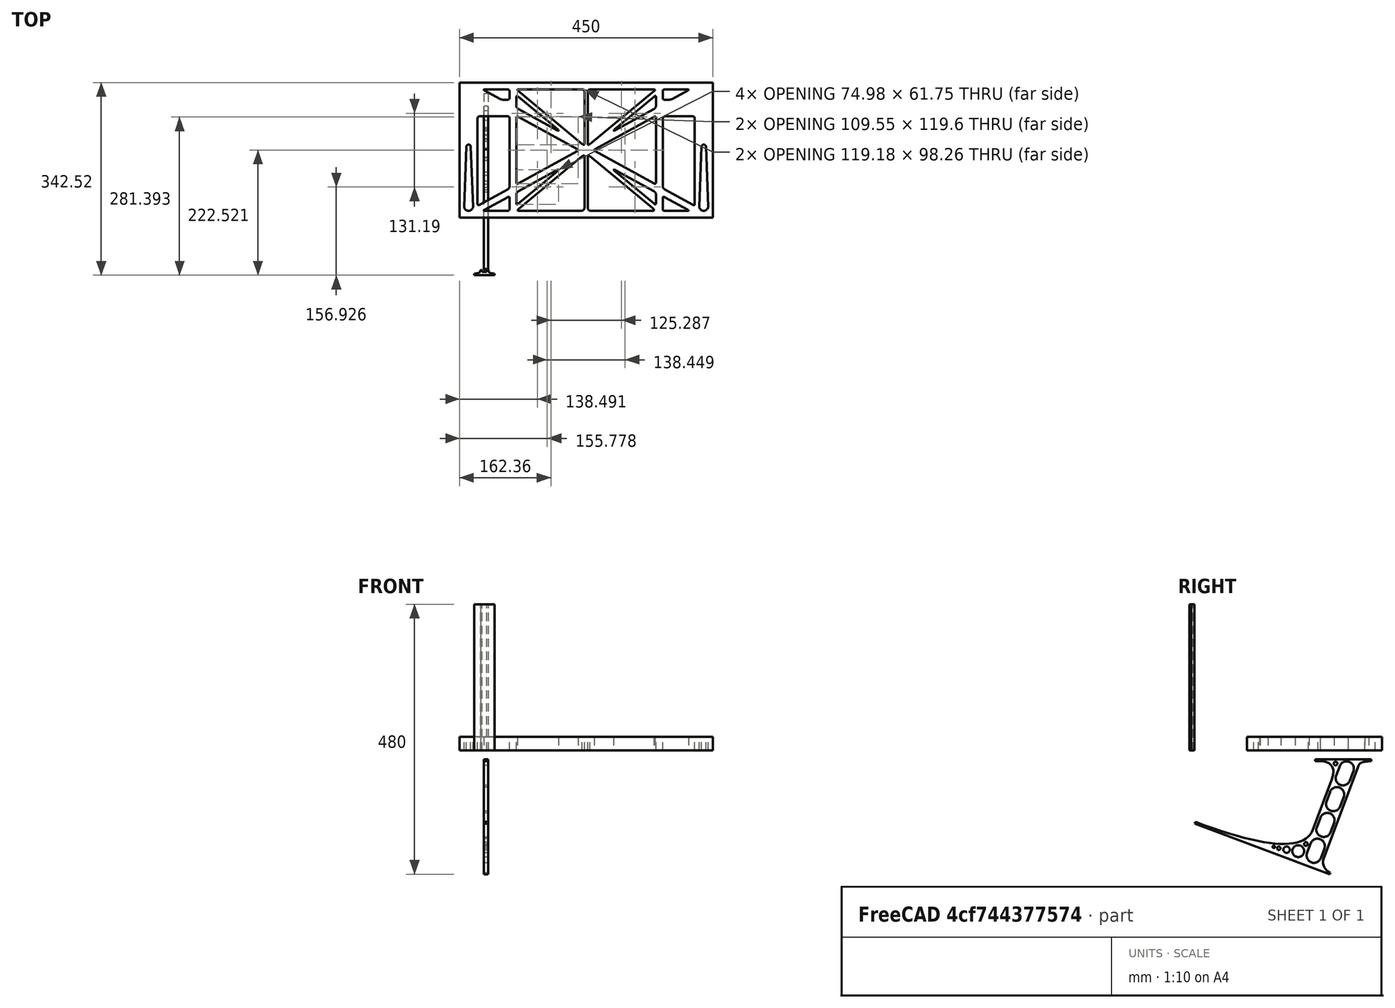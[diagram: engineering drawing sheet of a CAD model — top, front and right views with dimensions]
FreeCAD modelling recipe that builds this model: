
FCSTD DOCUMENT  (FreeCAD 0.19R0.19.2)
Label: laptopStand164FCStd
License: All rights reserved
LicenseURL: http://en.wikipedia.org/wiki/All_rights_reserved
objects: Sketcher::SketchObject×4, Part::Extrusion×3
note: 7 computed .brp shape members not serialized (recipe doc carries the construction recipe); baked Part::Feature solids carry a one-line shape summary decoded from their .brp

FEATURE [Sketcher::SketchObject] Sketch
  FullyConstrained = false
  sketch-geometry (349):
    g0: LineSegment StartX=-10.9272 StartY=-82.7794 StartZ=0 EndX=46.0728 EndY=-51.4823 EndZ=0
    g1: LineSegment StartX=-10.9272 StartY=76.4095 StartZ=0 EndX=-10.9272 EndY=-82.7794 EndZ=0
    g2: LineSegment StartX=46.0728 StartY=76.4095 StartZ=0 EndX=46.0728 EndY=-51.4823 EndZ=0
    g3: LineSegment StartX=-42.9272 StartY=136.221 StartZ=0 EndX=-42.9272 EndY=-103.779 EndZ=0
    g4: LineSegment StartX=407.073 StartY=136.221 StartZ=0 EndX=407.073 EndY=-103.779 EndZ=0
    g5: ArcOfCircle CenterX=-26.9272 CenterY=-83.7794 CenterZ=0 NormalX=0 NormalY=0 NormalZ=1 AngleXU=0 Radius=8 StartAngle=3.14159 EndAngle=6.28319
    g6: ArcOfCircle CenterX=391.073 CenterY=22.1087 CenterZ=0 NormalX=0 NormalY=0 NormalZ=1 AngleXU=0 Radius=8 StartAngle=-4.4e-15 EndAngle=3.14159
    g7: LineSegment StartX=399.073 StartY=22.1087 StartZ=0 EndX=399.073 EndY=-83.7794 EndZ=0
    g8: LineSegment StartX=383.073 StartY=22.1087 StartZ=0 EndX=383.073 EndY=-83.7794 EndZ=0
    g9: ArcOfCircle CenterX=391.073 CenterY=-83.7794 CenterZ=0 NormalX=0 NormalY=0 NormalZ=1 AngleXU=0 Radius=8 StartAngle=3.14159 EndAngle=6.28319
    g10: Circle CenterX=175.022 CenterY=27.0628 CenterZ=0 NormalX=0 NormalY=0 NormalZ=1 AngleXU=0 Radius=1
    g11: Circle CenterX=179.022 CenterY=24.8665 CenterZ=0 NormalX=0 NormalY=0 NormalZ=1 AngleXU=0 Radius=1
    g12: Circle CenterX=179.022 CenterY=27.0628 CenterZ=0 NormalX=0 NormalY=0 NormalZ=1 AngleXU=0 Radius=1
    g13: BSplineCurve PolesCount=3 KnotsCount=2 Degree=2 IsPeriodic=0
    g14: GeomPoint X=175.022 Y=27.0628 Z=0
    g15: GeomPoint X=179.022 Y=27.0628 Z=0
    g16: Circle CenterX=189.124 CenterY=27.0628 CenterZ=0 NormalX=0 NormalY=0 NormalZ=1 AngleXU=0 Radius=1
    g17: Circle CenterX=185.124 CenterY=24.8665 CenterZ=0 NormalX=0 NormalY=0 NormalZ=1 AngleXU=0 Radius=1
    g18: Circle CenterX=185.124 CenterY=27.0628 CenterZ=0 NormalX=0 NormalY=0 NormalZ=1 AngleXU=0 Radius=1
    g19: BSplineCurve PolesCount=3 KnotsCount=2 Degree=2 IsPeriodic=0
    g20: GeomPoint X=189.124 Y=27.0628 Z=0
    g21: GeomPoint X=185.124 Y=27.0628 Z=0
    g22: Circle CenterX=175.022 CenterY=5.37834 CenterZ=0 NormalX=0 NormalY=0 NormalZ=1 AngleXU=0 Radius=1
    g23: Circle CenterX=179.022 CenterY=7.57463 CenterZ=0 NormalX=0 NormalY=0 NormalZ=1 AngleXU=0 Radius=1
    g24: Circle CenterX=179.022 CenterY=5.34704 CenterZ=0 NormalX=0 NormalY=0 NormalZ=1 AngleXU=0 Radius=1
    g25: BSplineCurve PolesCount=3 KnotsCount=2 Degree=2 IsPeriodic=0
    g26: GeomPoint X=175.022 Y=5.37834 Z=0
    g27: GeomPoint X=179.022 Y=5.34704 Z=0
    g28: Circle CenterX=189.124 CenterY=5.37834 CenterZ=0 NormalX=0 NormalY=0 NormalZ=1 AngleXU=0 Radius=1
    g29: Circle CenterX=185.124 CenterY=7.57463 CenterZ=0 NormalX=0 NormalY=0 NormalZ=1 AngleXU=0 Radius=1
    g30: Circle CenterX=185.124 CenterY=5.34704 CenterZ=0 NormalX=0 NormalY=0 NormalZ=1 AngleXU=0 Radius=1
    g31: BSplineCurve PolesCount=3 KnotsCount=2 Degree=2 IsPeriodic=0
    g32: GeomPoint X=189.124 Y=5.37834 Z=0
    g33: GeomPoint X=185.124 Y=5.34704 Z=0
    g34: Circle CenterX=165.871 CenterY=18.1458 CenterZ=0 NormalX=0 NormalY=0 NormalZ=1 AngleXU=0 Radius=1
    g35: Circle CenterX=169.377 CenterY=16.2206 CenterZ=0 NormalX=0 NormalY=0 NormalZ=1 AngleXU=0 Radius=1
    g36: Circle CenterX=165.871 CenterY=14.2954 CenterZ=0 NormalX=0 NormalY=0 NormalZ=1 AngleXU=0 Radius=1
    g37: BSplineCurve PolesCount=3 KnotsCount=2 Degree=2 IsPeriodic=0
    g38: GeomPoint X=165.871 Y=18.1458 Z=0
    g39: GeomPoint X=165.871 Y=14.2954 Z=0
    g40: Circle CenterX=198.275 CenterY=18.1458 CenterZ=0 NormalX=0 NormalY=0 NormalZ=1 AngleXU=0 Radius=1
    g41: Circle CenterX=194.768 CenterY=16.2206 CenterZ=0 NormalX=0 NormalY=0 NormalZ=1 AngleXU=0 Radius=1
    g42: Circle CenterX=198.275 CenterY=14.2954 CenterZ=0 NormalX=0 NormalY=0 NormalZ=1 AngleXU=0 Radius=1
    g43: BSplineCurve PolesCount=3 KnotsCount=2 Degree=2 IsPeriodic=0
    g44: GeomPoint X=198.275 Y=18.1458 Z=0
    g45: GeomPoint X=198.275 Y=14.2954 Z=0
    g46: LineSegment StartX=407.073 StartY=-103.779 StartZ=0 EndX=-42.9272 EndY=-103.779 EndZ=0
    g47: LineSegment StartX=407.073 StartY=136.221 StartZ=0 EndX=-42.9272 EndY=136.221 EndZ=0
    g48: LineSegment StartX=46.0728 StartY=76.4095 StartZ=0 EndX=-10.9272 EndY=76.4095 EndZ=0
    g49: Circle CenterX=125.607 CenterY=54.1951 CenterZ=0 NormalX=0 NormalY=0 NormalZ=1 AngleXU=0 Radius=1
    g50: Circle CenterX=139.632 CenterY=46.4944 CenterZ=0 NormalX=0 NormalY=0 NormalZ=1 AngleXU=0 Radius=1
    g51: Circle CenterX=127.326 CenterY=56.7187 CenterZ=0 NormalX=0 NormalY=0 NormalZ=1 AngleXU=0 Radius=1
    g52: BSplineCurve PolesCount=3 KnotsCount=2 Degree=2 IsPeriodic=0
    g53: GeomPoint X=125.607 Y=54.1951 Z=0
    g54: GeomPoint X=127.326 Y=56.7187 Z=0
    g55: Circle CenterX=236.821 CenterY=56.7187 CenterZ=0 NormalX=0 NormalY=0 NormalZ=1 AngleXU=0 Radius=1
    g56: Circle CenterX=224.513 CenterY=46.4944 CenterZ=0 NormalX=0 NormalY=0 NormalZ=1 AngleXU=0 Radius=1
    g57: Circle CenterX=238.538 CenterY=54.1951 CenterZ=0 NormalX=0 NormalY=0 NormalZ=1 AngleXU=0 Radius=1
    g58: BSplineCurve PolesCount=3 KnotsCount=2 Degree=2 IsPeriodic=0
    g59: GeomPoint X=236.821 Y=56.7187 Z=0
    g60: GeomPoint X=238.538 Y=54.1951 Z=0
    g61: Circle CenterX=238.538 CenterY=-21.7539 CenterZ=0 NormalX=0 NormalY=0 NormalZ=1 AngleXU=0 Radius=1
    g62: Circle CenterX=224.513 CenterY=-14.0532 CenterZ=0 NormalX=0 NormalY=0 NormalZ=1 AngleXU=0 Radius=1
    g63: Circle CenterX=236.821 CenterY=-24.2775 CenterZ=0 NormalX=0 NormalY=0 NormalZ=1 AngleXU=0 Radius=1
    g64: BSplineCurve PolesCount=3 KnotsCount=2 Degree=2 IsPeriodic=0
    g65: GeomPoint X=238.538 Y=-21.7539 Z=0
    g66: GeomPoint X=236.821 Y=-24.2775 Z=0
    g67: Circle CenterX=125.607 CenterY=-21.7539 CenterZ=0 NormalX=0 NormalY=0 NormalZ=1 AngleXU=0 Radius=1
    g68: Circle CenterX=139.632 CenterY=-14.0532 CenterZ=0 NormalX=0 NormalY=0 NormalZ=1 AngleXU=0 Radius=1
    g69: Circle CenterX=127.325 CenterY=-24.2775 CenterZ=0 NormalX=0 NormalY=0 NormalZ=1 AngleXU=0 Radius=1
    g70: BSplineCurve PolesCount=3 KnotsCount=2 Degree=2 IsPeriodic=0
    g71: GeomPoint X=125.607 Y=-21.7539 Z=0
    g72: GeomPoint X=127.325 Y=-24.2775 Z=0
    g73: Circle CenterX=302.996 CenterY=111.695 CenterZ=0 NormalX=0 NormalY=0 NormalZ=1 AngleXU=0 Radius=1
    g74: Circle CenterX=306.073 CenterY=114.251 CenterZ=0 NormalX=0 NormalY=0 NormalZ=1 AngleXU=0 Radius=1
    g75: Circle CenterX=306.073 CenterY=110.251 CenterZ=0 NormalX=0 NormalY=0 NormalZ=1 AngleXU=0 Radius=1
    g76: BSplineCurve PolesCount=3 KnotsCount=2 Degree=2 IsPeriodic=0
    g77: GeomPoint X=302.996 Y=111.695 Z=0
    g78: GeomPoint X=306.073 Y=110.251 Z=0
    g79: Circle CenterX=306.073 CenterY=95.2763 CenterZ=0 NormalX=0 NormalY=0 NormalZ=1 AngleXU=0 Radius=1
    g80: Circle CenterX=306.073 CenterY=91.2763 CenterZ=0 NormalX=0 NormalY=0 NormalZ=1 AngleXU=0 Radius=1
    g81: Circle CenterX=302.567 CenterY=89.3511 CenterZ=0 NormalX=0 NormalY=0 NormalZ=1 AngleXU=0 Radius=1
    g82: BSplineCurve PolesCount=3 KnotsCount=2 Degree=2 IsPeriodic=0
    g83: GeomPoint X=306.073 Y=95.2763 Z=0
    g84: GeomPoint X=302.567 Y=89.3511 Z=0
    g85: LineSegment StartX=306.073 StartY=110.251 StartZ=0 EndX=306.073 EndY=95.2763 EndZ=0
    g86: LineSegment StartX=302.996 StartY=111.695 StartZ=0 EndX=236.821 EndY=56.7187 EndZ=0
    g87: LineSegment StartX=238.538 StartY=54.1951 StartZ=0 EndX=302.567 EndY=89.3511 EndZ=0
    g88: Circle CenterX=61.1496 CenterY=111.695 CenterZ=0 NormalX=0 NormalY=0 NormalZ=1 AngleXU=0 Radius=1
    g89: Circle CenterX=58.0728 CenterY=114.251 CenterZ=0 NormalX=0 NormalY=0 NormalZ=1 AngleXU=0 Radius=1
    g90: Circle CenterX=58.0728 CenterY=110.251 CenterZ=0 NormalX=0 NormalY=0 NormalZ=1 AngleXU=0 Radius=1
    g91: BSplineCurve PolesCount=3 KnotsCount=2 Degree=2 IsPeriodic=0
    g92: GeomPoint X=61.1496 Y=111.695 Z=0
    g93: GeomPoint X=58.0728 Y=110.251 Z=0
    g94: Circle CenterX=61.5791 CenterY=89.3511 CenterZ=0 NormalX=0 NormalY=0 NormalZ=1 AngleXU=0 Radius=1
    g95: Circle CenterX=58.0728 CenterY=91.2763 CenterZ=0 NormalX=0 NormalY=0 NormalZ=1 AngleXU=0 Radius=1
    g96: Circle CenterX=58.0728 CenterY=95.2763 CenterZ=0 NormalX=0 NormalY=0 NormalZ=1 AngleXU=0 Radius=1
    g97: BSplineCurve PolesCount=3 KnotsCount=2 Degree=2 IsPeriodic=0
    g98: GeomPoint X=61.5791 Y=89.3511 Z=0
    g99: GeomPoint X=58.0728 Y=95.2763 Z=0
    g100: LineSegment StartX=58.0728 StartY=110.251 StartZ=0 EndX=58.0728 EndY=95.2763 EndZ=0
    g101: LineSegment StartX=61.1496 StartY=111.695 StartZ=0 EndX=127.326 EndY=56.7187 EndZ=0
    g102: LineSegment StartX=125.607 StartY=54.1951 StartZ=0 EndX=61.5791 EndY=89.3511 EndZ=0
    g103: Circle CenterX=61.5791 CenterY=-56.9099 CenterZ=0 NormalX=0 NormalY=0 NormalZ=1 AngleXU=0 Radius=1
    g104: Circle CenterX=58.0728 CenterY=-58.8351 CenterZ=0 NormalX=0 NormalY=0 NormalZ=1 AngleXU=0 Radius=1
    g105: Circle CenterX=58.0728 CenterY=-62.8351 CenterZ=0 NormalX=0 NormalY=0 NormalZ=1 AngleXU=0 Radius=1
    g106: BSplineCurve PolesCount=3 KnotsCount=2 Degree=2 IsPeriodic=0
    g107: GeomPoint X=61.5791 Y=-56.9099 Z=0
    g108: GeomPoint X=58.0728 Y=-62.8351 Z=0
    g109: Circle CenterX=58.0728 CenterY=-77.8102 CenterZ=0 NormalX=0 NormalY=0 NormalZ=1 AngleXU=0 Radius=1
    g110: Circle CenterX=58.0728 CenterY=-81.8102 CenterZ=0 NormalX=0 NormalY=0 NormalZ=1 AngleXU=0 Radius=1
    g111: Circle CenterX=61.1496 CenterY=-79.2541 CenterZ=0 NormalX=0 NormalY=0 NormalZ=1 AngleXU=0 Radius=1
    g112: BSplineCurve PolesCount=3 KnotsCount=2 Degree=2 IsPeriodic=0
    g113: GeomPoint X=58.0728 Y=-77.8102 Z=0
    g114: GeomPoint X=61.1496 Y=-79.2541 Z=0
    g115: LineSegment StartX=58.0728 StartY=-62.8351 StartZ=0 EndX=58.0728 EndY=-77.8102 EndZ=0
    g116: LineSegment StartX=61.1496 StartY=-79.2541 StartZ=0 EndX=127.325 EndY=-24.2775 EndZ=0
    g117: LineSegment StartX=125.607 StartY=-21.7539 StartZ=0 EndX=61.5791 EndY=-56.9099 EndZ=0
    g118: Circle CenterX=302.567 CenterY=-56.9099 CenterZ=0 NormalX=0 NormalY=0 NormalZ=1 AngleXU=0 Radius=1
    g119: Circle CenterX=306.073 CenterY=-58.8351 CenterZ=0 NormalX=0 NormalY=0 NormalZ=1 AngleXU=0 Radius=1
    g120: Circle CenterX=306.073 CenterY=-62.8351 CenterZ=0 NormalX=0 NormalY=0 NormalZ=1 AngleXU=0 Radius=1
    g121: BSplineCurve PolesCount=3 KnotsCount=2 Degree=2 IsPeriodic=0
    g122: GeomPoint X=302.567 Y=-56.9099 Z=0
    g123: GeomPoint X=306.073 Y=-62.8351 Z=0
    g124: Circle CenterX=302.996 CenterY=-79.2541 CenterZ=0 NormalX=0 NormalY=0 NormalZ=1 AngleXU=0 Radius=1
    g125: Circle CenterX=306.073 CenterY=-81.8102 CenterZ=0 NormalX=0 NormalY=0 NormalZ=1 AngleXU=0 Radius=1
    g126: Circle CenterX=306.073 CenterY=-77.8102 CenterZ=0 NormalX=0 NormalY=0 NormalZ=1 AngleXU=0 Radius=1
    g127: BSplineCurve PolesCount=3 KnotsCount=2 Degree=2 IsPeriodic=0
    g128: GeomPoint X=302.996 Y=-79.2541 Z=0
    g129: GeomPoint X=306.073 Y=-77.8102 Z=0
    g130: LineSegment StartX=306.073 StartY=-62.8351 StartZ=0 EndX=306.073 EndY=-77.8102 EndZ=0
    g131: LineSegment StartX=302.996 StartY=-79.2541 StartZ=0 EndX=236.821 EndY=-24.2775 EndZ=0
    g132: LineSegment StartX=238.538 StartY=-21.7539 StartZ=0 EndX=302.567 EndY=-56.9099 EndZ=0
    g133: Circle CenterX=61.6457 CenterY=-88.8112 CenterZ=0 NormalX=0 NormalY=0 NormalZ=1 AngleXU=0 Radius=1
    g134: Circle CenterX=58.0728 CenterY=-91.7794 CenterZ=0 NormalX=0 NormalY=0 NormalZ=1 AngleXU=0 Radius=1
    g135: Circle CenterX=63.9135 CenterY=-91.7794 CenterZ=0 NormalX=0 NormalY=0 NormalZ=1 AngleXU=0 Radius=1
    g136: BSplineCurve PolesCount=3 KnotsCount=2 Degree=2 IsPeriodic=0
    g137: GeomPoint X=61.6457 Y=-88.8112 Z=0
    g138: GeomPoint X=63.9135 Y=-91.7794 Z=0
    g139: Circle CenterX=179.022 CenterY=-85.8163 CenterZ=0 NormalX=0 NormalY=0 NormalZ=1 AngleXU=0 Radius=1
    g140: Circle CenterX=179.022 CenterY=-91.7794 CenterZ=0 NormalX=0 NormalY=0 NormalZ=1 AngleXU=0 Radius=1
    g141: Circle CenterX=171.895 CenterY=-91.7794 CenterZ=0 NormalX=0 NormalY=0 NormalZ=1 AngleXU=0 Radius=1
    g142: BSplineCurve PolesCount=3 KnotsCount=2 Degree=2 IsPeriodic=0
    g143: GeomPoint X=179.022 Y=-85.8163 Z=0
    g144: GeomPoint X=171.895 Y=-91.7794 Z=0
    g145: Circle CenterX=185.124 CenterY=-86.2028 CenterZ=0 NormalX=0 NormalY=0 NormalZ=1 AngleXU=0 Radius=1
    g146: Circle CenterX=185.124 CenterY=-91.7794 CenterZ=0 NormalX=0 NormalY=0 NormalZ=1 AngleXU=0 Radius=1
    g147: Circle CenterX=191.747 CenterY=-91.7794 CenterZ=0 NormalX=0 NormalY=0 NormalZ=1 AngleXU=0 Radius=1
    g148: BSplineCurve PolesCount=3 KnotsCount=2 Degree=2 IsPeriodic=0
    g149: GeomPoint X=185.124 Y=-86.2028 Z=0
    g150: GeomPoint X=191.747 Y=-91.7794 Z=0
    g151: Circle CenterX=299.888 CenterY=-86.6413 CenterZ=0 NormalX=0 NormalY=0 NormalZ=1 AngleXU=0 Radius=1
    g152: Circle CenterX=306.073 CenterY=-91.7794 CenterZ=0 NormalX=0 NormalY=0 NormalZ=1 AngleXU=0 Radius=1
    g153: Circle CenterX=298.776 CenterY=-91.7794 CenterZ=0 NormalX=0 NormalY=0 NormalZ=1 AngleXU=0 Radius=1
    g154: BSplineCurve PolesCount=3 KnotsCount=2 Degree=2 IsPeriodic=0
    g155: GeomPoint X=299.888 Y=-86.6413 Z=0
    g156: GeomPoint X=298.776 Y=-91.7794 Z=0
    g157: LineSegment StartX=189.124 StartY=5.37834 StartZ=0 EndX=299.888 EndY=-86.6413 EndZ=0
    g158: LineSegment StartX=298.776 StartY=-91.7794 StartZ=0 EndX=191.747 EndY=-91.7794 EndZ=0
    g159: LineSegment StartX=185.124 StartY=-86.2028 StartZ=0 EndX=185.124 EndY=5.34704 EndZ=0
    g160: LineSegment StartX=179.022 StartY=5.34704 StartZ=0 EndX=179.022 EndY=-85.8163 EndZ=0
    g161: LineSegment StartX=171.895 StartY=-91.7794 StartZ=0 EndX=63.9135 EndY=-91.7794 EndZ=0
    g162: LineSegment StartX=61.6457 StartY=-88.8112 StartZ=0 EndX=175.022 EndY=5.37834 EndZ=0
    g163: Circle CenterX=302.073 CenterY=124.221 CenterZ=0 NormalX=0 NormalY=0 NormalZ=1 AngleXU=0 Radius=1
    g164: Circle CenterX=306.073 CenterY=124.221 CenterZ=0 NormalX=0 NormalY=0 NormalZ=1 AngleXU=0 Radius=1
    g165: Circle CenterX=302.996 CenterY=121.665 CenterZ=0 NormalX=0 NormalY=0 NormalZ=1 AngleXU=0 Radius=1
    g166: BSplineCurve PolesCount=3 KnotsCount=2 Degree=2 IsPeriodic=0
    g167: GeomPoint X=302.073 Y=124.221 Z=0
    g168: GeomPoint X=302.996 Y=121.665 Z=0
    g169: Circle CenterX=189.124 CenterY=124.221 CenterZ=0 NormalX=0 NormalY=0 NormalZ=1 AngleXU=0 Radius=1
    g170: Circle CenterX=185.124 CenterY=124.221 CenterZ=0 NormalX=0 NormalY=0 NormalZ=1 AngleXU=0 Radius=1
    g171: Circle CenterX=185.124 CenterY=120.221 CenterZ=0 NormalX=0 NormalY=0 NormalZ=1 AngleXU=0 Radius=1
    g172: BSplineCurve PolesCount=3 KnotsCount=2 Degree=2 IsPeriodic=0
    g173: GeomPoint X=189.124 Y=124.221 Z=0
    g174: GeomPoint X=185.124 Y=120.221 Z=0
    g175: Circle CenterX=175.022 CenterY=124.221 CenterZ=0 NormalX=0 NormalY=0 NormalZ=1 AngleXU=0 Radius=1
    g176: Circle CenterX=179.022 CenterY=124.221 CenterZ=0 NormalX=0 NormalY=0 NormalZ=1 AngleXU=0 Radius=1
    g177: Circle CenterX=179.022 CenterY=120.221 CenterZ=0 NormalX=0 NormalY=0 NormalZ=1 AngleXU=0 Radius=1
    g178: BSplineCurve PolesCount=3 KnotsCount=2 Degree=2 IsPeriodic=0
    g179: GeomPoint X=175.022 Y=124.221 Z=0
    g180: GeomPoint X=179.022 Y=120.221 Z=0
    g181: Circle CenterX=62.0728 CenterY=124.221 CenterZ=0 NormalX=0 NormalY=0 NormalZ=1 AngleXU=0 Radius=1
    g182: Circle CenterX=58.0728 CenterY=124.221 CenterZ=0 NormalX=0 NormalY=0 NormalZ=1 AngleXU=0 Radius=1
    g183: Circle CenterX=61.1496 CenterY=121.665 CenterZ=0 NormalX=0 NormalY=0 NormalZ=1 AngleXU=0 Radius=1
    g184: BSplineCurve PolesCount=3 KnotsCount=2 Degree=2 IsPeriodic=0
    g185: GeomPoint X=62.0728 Y=124.221 Z=0
    g186: GeomPoint X=61.1496 Y=121.665 Z=0
    g187: LineSegment StartX=62.0728 StartY=124.221 StartZ=0 EndX=175.022 EndY=124.221 EndZ=0
    g188: LineSegment StartX=179.022 StartY=120.221 StartZ=0 EndX=179.022 EndY=27.0628 EndZ=0
    g189: LineSegment StartX=185.124 StartY=27.0628 StartZ=0 EndX=185.124 EndY=120.221 EndZ=0
    g190: LineSegment StartX=189.124 StartY=124.221 StartZ=0 EndX=302.073 EndY=124.221 EndZ=0
    g191: LineSegment StartX=302.996 StartY=121.665 StartZ=0 EndX=189.124 EndY=27.0628 EndZ=0
    g192: LineSegment StartX=175.022 StartY=27.0628 StartZ=0 EndX=61.1496 EndY=121.665 EndZ=0
    g193: Circle CenterX=61.5791 CenterY=75.4095 CenterZ=0 NormalX=0 NormalY=0 NormalZ=1 AngleXU=0 Radius=1
    g194: Circle CenterX=58.0728 CenterY=77.3346 CenterZ=0 NormalX=0 NormalY=0 NormalZ=1 AngleXU=0 Radius=1
    g195: Circle CenterX=58.0728 CenterY=73.3346 CenterZ=0 NormalX=0 NormalY=0 NormalZ=1 AngleXU=0 Radius=1
    g196: BSplineCurve PolesCount=3 KnotsCount=2 Degree=2 IsPeriodic=0
    g197: GeomPoint X=61.5791 Y=75.4095 Z=0
    g198: GeomPoint X=58.0728 Y=73.3346 Z=0
    g199: Circle CenterX=58.0728 CenterY=-40.8935 CenterZ=0 NormalX=0 NormalY=0 NormalZ=1 AngleXU=0 Radius=1
    g200: Circle CenterX=58.0728 CenterY=-44.8935 CenterZ=0 NormalX=0 NormalY=0 NormalZ=1 AngleXU=0 Radius=1
    g201: Circle CenterX=61.5791 CenterY=-42.9683 CenterZ=0 NormalX=0 NormalY=0 NormalZ=1 AngleXU=0 Radius=1
    g202: BSplineCurve PolesCount=3 KnotsCount=2 Degree=2 IsPeriodic=0
    g203: GeomPoint X=58.0728 Y=-40.8935 Z=0
    g204: GeomPoint X=61.5791 Y=-42.9683 Z=0
    g205: LineSegment StartX=61.5791 StartY=-42.9683 StartZ=0 EndX=165.871 EndY=14.2954 EndZ=0
    g206: LineSegment StartX=165.871 StartY=18.1458 StartZ=0 EndX=61.5791 EndY=75.4095 EndZ=0
    g207: LineSegment StartX=58.0728 StartY=73.3346 StartZ=0 EndX=58.0728 EndY=-40.8935 EndZ=0
    g208: Circle CenterX=302.567 CenterY=-42.9683 CenterZ=0 NormalX=0 NormalY=0 NormalZ=1 AngleXU=0 Radius=1
    g209: Circle CenterX=306.073 CenterY=-44.8935 CenterZ=0 NormalX=0 NormalY=0 NormalZ=1 AngleXU=0 Radius=1
    g210: Circle CenterX=306.073 CenterY=-40.8935 CenterZ=0 NormalX=0 NormalY=0 NormalZ=1 AngleXU=0 Radius=1
    g211: BSplineCurve PolesCount=3 KnotsCount=2 Degree=2 IsPeriodic=0
    g212: GeomPoint X=302.567 Y=-42.9683 Z=0
    g213: GeomPoint X=306.073 Y=-40.8935 Z=0
    g214: Circle CenterX=306.073 CenterY=73.3346 CenterZ=0 NormalX=0 NormalY=0 NormalZ=1 AngleXU=0 Radius=1
    g215: Circle CenterX=306.073 CenterY=77.3346 CenterZ=0 NormalX=0 NormalY=0 NormalZ=1 AngleXU=0 Radius=1
    g216: Circle CenterX=302.567 CenterY=75.4095 CenterZ=0 NormalX=0 NormalY=0 NormalZ=1 AngleXU=0 Radius=1
    g217: BSplineCurve PolesCount=3 KnotsCount=2 Degree=2 IsPeriodic=0
    g218: GeomPoint X=306.073 Y=73.3346 Z=0
    g219: GeomPoint X=302.567 Y=75.4095 Z=0
    g220: LineSegment StartX=302.567 StartY=-42.9683 StartZ=0 EndX=198.275 EndY=14.2954 EndZ=0
    g221: LineSegment StartX=198.275 StartY=18.1458 StartZ=0 EndX=302.567 EndY=75.4095 EndZ=0
    g222: LineSegment StartX=306.073 StartY=73.3346 StartZ=0 EndX=306.073 EndY=-40.8935 EndZ=0
    g223: LineSegment StartX=322.073 StartY=105.865 StartZ=0 EndX=328.643 EndY=105.865 EndZ=0
    g224: LineSegment StartX=318.073 StartY=120.221 StartZ=0 EndX=318.073 EndY=109.865 EndZ=0
    g225: LineSegment StartX=336.157 StartY=107.779 StartZ=0 EndX=362.567 EndY=122.294 EndZ=0
    g226: Circle CenterX=362.073 CenterY=124.221 CenterZ=0 NormalX=0 NormalY=0 NormalZ=1 AngleXU=0 Radius=1
    g227: Circle CenterX=366.073 CenterY=124.221 CenterZ=0 NormalX=0 NormalY=0 NormalZ=1 AngleXU=0 Radius=1
    g228: Circle CenterX=362.567 CenterY=122.294 CenterZ=0 NormalX=0 NormalY=0 NormalZ=1 AngleXU=0 Radius=1
    g229: BSplineCurve PolesCount=3 KnotsCount=2 Degree=2 IsPeriodic=0
    g230: GeomPoint X=362.073 Y=124.221 Z=0
    g231: GeomPoint X=362.567 Y=122.294 Z=0
    g232: Circle CenterX=322.073 CenterY=124.221 CenterZ=0 NormalX=0 NormalY=0 NormalZ=1 AngleXU=0 Radius=1
    g233: Circle CenterX=318.073 CenterY=124.221 CenterZ=0 NormalX=0 NormalY=0 NormalZ=1 AngleXU=0 Radius=1
    g234: Circle CenterX=318.073 CenterY=120.221 CenterZ=0 NormalX=0 NormalY=0 NormalZ=1 AngleXU=0 Radius=1
    g235: BSplineCurve PolesCount=3 KnotsCount=2 Degree=2 IsPeriodic=0
    g236: GeomPoint X=322.073 Y=124.221 Z=0
    g237: GeomPoint X=318.073 Y=120.221 Z=0
    g238: Circle CenterX=322.073 CenterY=105.865 CenterZ=0 NormalX=0 NormalY=0 NormalZ=1 AngleXU=0 Radius=1
    g239: Circle CenterX=318.073 CenterY=105.865 CenterZ=0 NormalX=0 NormalY=0 NormalZ=1 AngleXU=0 Radius=1
    g240: Circle CenterX=318.073 CenterY=109.865 CenterZ=0 NormalX=0 NormalY=0 NormalZ=1 AngleXU=0 Radius=1
    g241: BSplineCurve PolesCount=3 KnotsCount=2 Degree=2 IsPeriodic=0
    g242: GeomPoint X=322.073 Y=105.865 Z=0
    g243: GeomPoint X=318.073 Y=109.865 Z=0
    g244: Circle CenterX=336.157 CenterY=107.779 CenterZ=0 NormalX=0 NormalY=0 NormalZ=1 AngleXU=0 Radius=1
    g245: Circle CenterX=332.651 CenterY=105.853 CenterZ=0 NormalX=0 NormalY=0 NormalZ=1 AngleXU=0 Radius=1
    g246: Circle CenterX=328.643 CenterY=105.865 CenterZ=0 NormalX=0 NormalY=0 NormalZ=1 AngleXU=0 Radius=1
    g247: BSplineCurve PolesCount=3 KnotsCount=2 Degree=2 IsPeriodic=0
    g248: GeomPoint X=336.157 Y=107.779 Z=0
    g249: GeomPoint X=328.643 Y=105.865 Z=0
    g250: LineSegment StartX=322.073 StartY=124.221 StartZ=0 EndX=362.073 EndY=124.221 EndZ=0
    g251: Circle CenterX=371.567 CenterY=-80.8644 CenterZ=0 NormalX=0 NormalY=0 NormalZ=1 AngleXU=0 Radius=1
    g252: Circle CenterX=375.073 CenterY=-82.7896 CenterZ=0 NormalX=0 NormalY=0 NormalZ=1 AngleXU=0 Radius=1
    g253: Circle CenterX=375.073 CenterY=-78.7896 CenterZ=0 NormalX=0 NormalY=0 NormalZ=1 AngleXU=0 Radius=1
    g254: BSplineCurve PolesCount=3 KnotsCount=2 Degree=2 IsPeriodic=0
    g255: GeomPoint X=371.567 Y=-80.8644 Z=0
    g256: GeomPoint X=375.073 Y=-78.7896 Z=0
    g257: Circle CenterX=321.579 CenterY=-53.4075 CenterZ=0 NormalX=0 NormalY=0 NormalZ=1 AngleXU=0 Radius=1
    g258: Circle CenterX=318.073 CenterY=-51.4823 CenterZ=0 NormalX=0 NormalY=0 NormalZ=1 AngleXU=0 Radius=1
    g259: Circle CenterX=318.073 CenterY=-47.4805 CenterZ=0 NormalX=0 NormalY=0 NormalZ=1 AngleXU=0 Radius=1
    g260: BSplineCurve PolesCount=3 KnotsCount=2 Degree=2 IsPeriodic=0
    g261: GeomPoint X=321.579 Y=-53.4075 Z=0
    g262: GeomPoint X=318.073 Y=-47.4805 Z=0
    g263: LineSegment StartX=371.567 StartY=-80.8644 StartZ=0 EndX=321.579 EndY=-53.4075 EndZ=0
    g264: Circle CenterX=321.579 CenterY=-67.3492 CenterZ=0 NormalX=0 NormalY=0 NormalZ=1 AngleXU=0 Radius=1
    g265: Circle CenterX=318.073 CenterY=-65.424 CenterZ=0 NormalX=0 NormalY=0 NormalZ=1 AngleXU=0 Radius=1
    g266: Circle CenterX=318.073 CenterY=-69.424 CenterZ=0 NormalX=0 NormalY=0 NormalZ=1 AngleXU=0 Radius=1
    g267: BSplineCurve PolesCount=3 KnotsCount=2 Degree=2 IsPeriodic=0
    g268: GeomPoint X=321.579 Y=-67.3492 Z=0
    g269: GeomPoint X=318.073 Y=-69.424 Z=0
    g270: Circle CenterX=362.567 CenterY=-89.8542 CenterZ=0 NormalX=0 NormalY=0 NormalZ=1 AngleXU=0 Radius=1
    g271: Circle CenterX=366.073 CenterY=-91.7794 CenterZ=0 NormalX=0 NormalY=0 NormalZ=1 AngleXU=0 Radius=1
    g272: Circle CenterX=362.073 CenterY=-91.7794 CenterZ=0 NormalX=0 NormalY=0 NormalZ=1 AngleXU=0 Radius=1
    g273: BSplineCurve PolesCount=3 KnotsCount=2 Degree=2 IsPeriodic=0
    g274: GeomPoint X=362.567 Y=-89.8542 Z=0
    g275: GeomPoint X=362.073 Y=-91.7794 Z=0
    g276: Circle CenterX=322.073 CenterY=-91.7794 CenterZ=0 NormalX=0 NormalY=0 NormalZ=1 AngleXU=0 Radius=1
    g277: Circle CenterX=318.073 CenterY=-91.7794 CenterZ=0 NormalX=0 NormalY=0 NormalZ=1 AngleXU=0 Radius=1
    g278: Circle CenterX=318.073 CenterY=-87.7794 CenterZ=0 NormalX=0 NormalY=0 NormalZ=1 AngleXU=0 Radius=1
    g279: BSplineCurve PolesCount=3 KnotsCount=2 Degree=2 IsPeriodic=0
    g280: GeomPoint X=322.073 Y=-91.7794 Z=0
    g281: GeomPoint X=318.073 Y=-87.7794 Z=0
    g282: LineSegment StartX=362.567 StartY=-89.8542 StartZ=0 EndX=321.579 EndY=-67.3492 EndZ=0
    g283: LineSegment StartX=318.073 StartY=-69.424 StartZ=0 EndX=318.073 EndY=-87.7794 EndZ=0
    g284: LineSegment StartX=322.073 StartY=-91.7794 StartZ=0 EndX=362.073 EndY=-91.7794 EndZ=0
    g285: Circle CenterX=2.07281 CenterY=124.221 CenterZ=0 NormalX=0 NormalY=0 NormalZ=1 AngleXU=0 Radius=1
    g286: Circle CenterX=1.57905 CenterY=122.295 CenterZ=0 NormalX=0 NormalY=0 NormalZ=1 AngleXU=0 Radius=1
    g287: BSplineCurve PolesCount=3 KnotsCount=2 Degree=2 IsPeriodic=0
    g288: GeomPoint X=2.07281 Y=124.221 Z=0
    g289: GeomPoint X=1.57905 Y=122.295 Z=0
    g290: Circle CenterX=42.0728 CenterY=124.221 CenterZ=0 NormalX=0 NormalY=0 NormalZ=1 AngleXU=0 Radius=1
    g291: Circle CenterX=46.0728 CenterY=124.221 CenterZ=0 NormalX=0 NormalY=0 NormalZ=1 AngleXU=0 Radius=1
    g292: Circle CenterX=46.0728 CenterY=120.221 CenterZ=0 NormalX=0 NormalY=0 NormalZ=1 AngleXU=0 Radius=1
    g293: BSplineCurve PolesCount=3 KnotsCount=2 Degree=2 IsPeriodic=0
    g294: GeomPoint X=42.0728 Y=124.221 Z=0
    g295: GeomPoint X=46.0728 Y=120.221 Z=0
    g296: Circle CenterX=46.0728 CenterY=109.865 CenterZ=0 NormalX=0 NormalY=0 NormalZ=1 AngleXU=0 Radius=1
    g297: Circle CenterX=46.0728 CenterY=105.865 CenterZ=0 NormalX=0 NormalY=0 NormalZ=1 AngleXU=0 Radius=1
    g298: Circle CenterX=42.0728 CenterY=105.865 CenterZ=0 NormalX=0 NormalY=0 NormalZ=1 AngleXU=0 Radius=1
    g299: BSplineCurve PolesCount=3 KnotsCount=2 Degree=2 IsPeriodic=0
    g300: GeomPoint X=46.0728 Y=109.865 Z=0
    g301: GeomPoint X=42.0728 Y=105.865 Z=0
    g302: Circle CenterX=35.5028 CenterY=105.865 CenterZ=0 NormalX=0 NormalY=0 NormalZ=1 AngleXU=0 Radius=1
    g303: Circle CenterX=31.5028 CenterY=105.865 CenterZ=0 NormalX=0 NormalY=0 NormalZ=1 AngleXU=0 Radius=1
    g304: Circle CenterX=27.9965 CenterY=107.79 CenterZ=0 NormalX=0 NormalY=0 NormalZ=1 AngleXU=0 Radius=1
    g305: BSplineCurve PolesCount=3 KnotsCount=2 Degree=2 IsPeriodic=0
    g306: GeomPoint X=35.5028 Y=105.865 Z=0
    g307: GeomPoint X=27.9965 Y=107.79 Z=0
    g308: LineSegment StartX=2.07281 StartY=124.221 StartZ=0 EndX=42.0728 EndY=124.221 EndZ=0
    g309: LineSegment StartX=46.0728 StartY=120.221 StartZ=0 EndX=46.0728 EndY=109.865 EndZ=0
    g310: LineSegment StartX=42.0728 StartY=105.865 StartZ=0 EndX=35.5028 EndY=105.865 EndZ=0
    g311: LineSegment StartX=27.9965 StartY=107.79 StartZ=0 EndX=1.57905 EndY=122.295 EndZ=0
    g312: Circle CenterX=42.5666 CenterY=-67.3492 CenterZ=0 NormalX=0 NormalY=0 NormalZ=1 AngleXU=0 Radius=1
    g313: Circle CenterX=46.0728 CenterY=-65.424 CenterZ=0 NormalX=0 NormalY=0 NormalZ=1 AngleXU=0 Radius=1
    g314: Circle CenterX=46.0728 CenterY=-69.424 CenterZ=0 NormalX=0 NormalY=0 NormalZ=1 AngleXU=0 Radius=1
    g315: BSplineCurve PolesCount=3 KnotsCount=2 Degree=2 IsPeriodic=0
    g316: GeomPoint X=42.5666 Y=-67.3492 Z=0
    g317: GeomPoint X=46.0728 Y=-69.424 Z=0
    g318: Circle CenterX=46.0728 CenterY=-87.7794 CenterZ=0 NormalX=0 NormalY=0 NormalZ=1 AngleXU=0 Radius=1
    g319: Circle CenterX=46.0728 CenterY=-91.7794 CenterZ=0 NormalX=0 NormalY=0 NormalZ=1 AngleXU=0 Radius=1
    g320: Circle CenterX=42.0728 CenterY=-91.7794 CenterZ=0 NormalX=0 NormalY=0 NormalZ=1 AngleXU=0 Radius=1
    g321: BSplineCurve PolesCount=3 KnotsCount=2 Degree=2 IsPeriodic=0
    g322: GeomPoint X=46.0728 Y=-87.7794 Z=0
    g323: GeomPoint X=42.0728 Y=-91.7794 Z=0
    g324: Circle CenterX=2.07281 CenterY=-91.7794 CenterZ=0 NormalX=0 NormalY=0 NormalZ=1 AngleXU=0 Radius=1
    g325: Circle CenterX=-1.92719 CenterY=-91.7794 CenterZ=0 NormalX=0 NormalY=0 NormalZ=1 AngleXU=0 Radius=1
    g326: Circle CenterX=1.57905 CenterY=-89.8542 CenterZ=0 NormalX=0 NormalY=0 NormalZ=1 AngleXU=0 Radius=1
    g327: BSplineCurve PolesCount=3 KnotsCount=2 Degree=2 IsPeriodic=0
    g328: GeomPoint X=2.07281 Y=-91.7794 Z=0
    g329: GeomPoint X=1.57905 Y=-89.8542 Z=0
    g330: LineSegment StartX=2.07281 StartY=-91.7794 StartZ=0 EndX=42.0728 EndY=-91.7794 EndZ=0
    g331: LineSegment StartX=46.0728 StartY=-87.7794 StartZ=0 EndX=46.0728 EndY=-69.424 EndZ=0
    g332: LineSegment StartX=42.5666 StartY=-67.3492 StartZ=0 EndX=1.57905 EndY=-89.8542 EndZ=0
    g333: Circle CenterX=322.073 CenterY=76.4095 CenterZ=0 NormalX=0 NormalY=0 NormalZ=1 AngleXU=0 Radius=4
    g334: BSplineCurve PolesCount=3 KnotsCount=2 Degree=2 IsPeriodic=0
    g335: GeomPoint X=318.073 Y=72.4095 Z=0
    g336: GeomPoint X=322.073 Y=76.4095 Z=0
    g337: Circle CenterX=375.073 CenterY=72.4095 CenterZ=0 NormalX=0 NormalY=0 NormalZ=1 AngleXU=0 Radius=1
    g338: Circle CenterX=375.073 CenterY=76.4095 CenterZ=0 NormalX=0 NormalY=0 NormalZ=1 AngleXU=0 Radius=1
    g339: Circle CenterX=371.073 CenterY=76.4095 CenterZ=0 NormalX=0 NormalY=0 NormalZ=1 AngleXU=0 Radius=1
    g340: BSplineCurve PolesCount=3 KnotsCount=2 Degree=2 IsPeriodic=0
    g341: GeomPoint X=375.073 Y=72.4095 Z=0
    g342: GeomPoint X=371.073 Y=76.4095 Z=0
    g343: LineSegment StartX=322.073 StartY=76.4095 StartZ=0 EndX=371.073 EndY=76.4095 EndZ=0
    g344: LineSegment StartX=318.073 StartY=72.4095 StartZ=0 EndX=318.073 EndY=-47.4805 EndZ=0
    g345: LineSegment StartX=375.073 StartY=72.4095 StartZ=0 EndX=375.073 EndY=-78.7896 EndZ=0
    g346: ArcOfCircle CenterX=-26.9272 CenterY=22.1087 CenterZ=0 NormalX=0 NormalY=0 NormalZ=1 AngleXU=0 Radius=4 StartAngle=5e-16 EndAngle=3.14159
    g347: LineSegment StartX=-30.9272 StartY=22.1087 StartZ=0 EndX=-34.9272 EndY=-83.7794 EndZ=0
    g348: LineSegment StartX=-18.9272 StartY=-83.7794 StartZ=0 EndX=-22.9272 EndY=22.1087 EndZ=0
  constraints (572):
    c: Coincident(g0,g2)
    c: Block(g0)
    c: Block(g1)
    c: Vertical(g3)
    c: Vertical(g4)
    c: Block(g4)
    c: Block(g3)
    c: Tangent(g6,g7) = 1.5708
    c: Tangent(g7,g9) = 1.5708
    c: Equal(g6,g9)
    c: Coincident(g8,g6)
    c: Coincident(g8,g9)
    c: Block(g7)
    c: Block(g8)
    c: Weight(g10) = 1
    c: Equal(g10,g11)
    c: Equal(g10,g12)
    c: InternalAlignment(g10,g13)
    c: InternalAlignment(g11,g13)
    c: InternalAlignment(g12,g13)
    c: InternalAlignment(g14,g13)
    c: InternalAlignment(g15,g13)
    c: Weight(g16) = 1
    c: Equal(g16,g17)
    c: Equal(g16,g18)
    c: InternalAlignment(g16,g19)
    c: InternalAlignment(g17,g19)
    c: InternalAlignment(g18,g19)
    c: InternalAlignment(g20,g19)
    c: InternalAlignment(g21,g19)
    c: Block(g19)
    c: Block(g13)
    c: Weight(g22) = 1
    c: Equal(g22,g23)
    c: Equal(g22,g24)
    c: InternalAlignment(g22,g25)
    c: InternalAlignment(g23,g25)
    c: InternalAlignment(g24,g25)
    c: InternalAlignment(g26,g25)
    c: InternalAlignment(g27,g25)
    c: Weight(g28) = 1
    c: Equal(g28,g29)
    c: Equal(g28,g30)
    c: InternalAlignment(g28,g31)
    c: InternalAlignment(g29,g31)
    c: InternalAlignment(g30,g31)
    c: InternalAlignment(g32,g31)
    c: InternalAlignment(g33,g31)
    c: Block(g31)
    c: Block(g25)
    c: Weight(g34) = 1
    c: Equal(g34,g35)
    c: Equal(g34,g36)
    c: InternalAlignment(g34,g37)
    c: InternalAlignment(g35,g37)
    c: InternalAlignment(g36,g37)
    c: InternalAlignment(g38,g37)
    c: InternalAlignment(g39,g37)
    c: Weight(g40) = 1
    c: Equal(g40,g41)
    c: Equal(g40,g42)
    c: InternalAlignment(g40,g43)
    c: InternalAlignment(g41,g43)
    c: InternalAlignment(g42,g43)
    c: InternalAlignment(g44,g43)
    c: InternalAlignment(g45,g43)
    c: Block(g37)
    c: Block(g43)
    c: Coincident(g46,g4)
    c: Coincident(g46,g3)
    c: Horizontal(g46)
    c: Distance(g46) = 450
    c: Coincident(g47,g4)
    c: Coincident(g47,g3)
    c: Horizontal(g47)
    c: Horizontal(g48)
    c: Coincident(g2,g48)
    c: Block(g48)
    c: Coincident(g1,g48)
    c: Weight(g49) = 1
    c: Equal(g49,g50)
    c: Equal(g49,g51)
    c: InternalAlignment(g49,g52)
    c: InternalAlignment(g50,g52)
    c: InternalAlignment(g51,g52)
    c: InternalAlignment(g53,g52)
    c: InternalAlignment(g54,g52)
    c: Block(g52)
    c: Weight(g55) = 1
    c: Equal(g55,g56)
    c: Equal(g55,g57)
    c: InternalAlignment(g55,g58)
    c: InternalAlignment(g56,g58)
    c: InternalAlignment(g57,g58)
    c: InternalAlignment(g59,g58)
    c: InternalAlignment(g60,g58)
    c: Block(g58)
    c: Weight(g61) = 1
    c: Equal(g61,g62)
    c: Equal(g61,g63)
    c: InternalAlignment(g61,g64)
    c: InternalAlignment(g62,g64)
    c: InternalAlignment(g63,g64)
    c: InternalAlignment(g65,g64)
    c: InternalAlignment(g66,g64)
    c: Block(g64)
    c: Weight(g67) = 1
    c: Equal(g67,g68)
    c: Equal(g67,g69)
    c: InternalAlignment(g67,g70)
    c: InternalAlignment(g68,g70)
    c: InternalAlignment(g69,g70)
    c: InternalAlignment(g71,g70)
    c: InternalAlignment(g72,g70)
    c: Block(g70)
    c: Weight(g73) = 1
    c: Equal(g73,g74)
    c: Equal(g73,g75)
    c: InternalAlignment(g73,g76)
    c: InternalAlignment(g74,g76)
    c: InternalAlignment(g75,g76)
    c: InternalAlignment(g77,g76)
    c: InternalAlignment(g78,g76)
    c: Weight(g79) = 1
    c: Equal(g79,g80)
    c: Equal(g79,g81)
    c: InternalAlignment(g79,g82)
    c: InternalAlignment(g80,g82)
    c: InternalAlignment(g81,g82)
    c: InternalAlignment(g83,g82)
    c: InternalAlignment(g84,g82)
    c: Block(g76)
    c: Block(g82)
    c: Coincident(g85,g76)
    c: Coincident(g85,g82)
    c: Vertical(g85)
    c: Coincident(g86,g76)
    c: Coincident(g86,g58)
    c: Coincident(g87,g58)
    c: Coincident(g87,g82)
    c: Weight(g88) = 1
    c: Equal(g88,g89)
    c: Equal(g88,g90)
    c: InternalAlignment(g88,g91)
    c: InternalAlignment(g89,g91)
    c: InternalAlignment(g90,g91)
    c: InternalAlignment(g92,g91)
    c: InternalAlignment(g93,g91)
    c: Weight(g94) = 1
    c: Equal(g94,g95)
    c: Equal(g94,g96)
    c: InternalAlignment(g94,g97)
    c: InternalAlignment(g95,g97)
    c: InternalAlignment(g96,g97)
    c: InternalAlignment(g98,g97)
    c: InternalAlignment(g99,g97)
    c: Block(g91)
    c: Block(g97)
    c: Coincident(g100,g91)
    c: Coincident(g100,g97)
    c: Vertical(g100)
    c: Coincident(g101,g91)
    c: Coincident(g101,g52)
    c: Coincident(g102,g52)
    c: Coincident(g102,g97)
    c: Weight(g103) = 1
    c: Equal(g103,g104)
    c: Equal(g103,g105)
    c: InternalAlignment(g103,g106)
    c: InternalAlignment(g104,g106)
    c: InternalAlignment(g105,g106)
    c: InternalAlignment(g107,g106)
    c: InternalAlignment(g108,g106)
    c: Weight(g109) = 1
    c: Equal(g109,g110)
    c: Equal(g109,g111)
    c: InternalAlignment(g109,g112)
    c: InternalAlignment(g110,g112)
    c: InternalAlignment(g111,g112)
    c: InternalAlignment(g113,g112)
    c: InternalAlignment(g114,g112)
    c: Block(g106)
    c: Block(g112)
    c: Coincident(g115,g106)
    c: Coincident(g115,g112)
    c: Vertical(g115)
    c: Coincident(g116,g112)
    c: Coincident(g116,g70)
    c: Coincident(g117,g70)
    c: Coincident(g117,g106)
    c: Weight(g118) = 1
    c: Equal(g118,g119)
    c: Equal(g118,g120)
    c: InternalAlignment(g118,g121)
    c: InternalAlignment(g119,g121)
    c: InternalAlignment(g120,g121)
    c: InternalAlignment(g122,g121)
    c: InternalAlignment(g123,g121)
    c: Weight(g124) = 1
    c: Equal(g124,g125)
    c: Equal(g124,g126)
    c: InternalAlignment(g124,g127)
    c: InternalAlignment(g125,g127)
    c: InternalAlignment(g126,g127)
    c: InternalAlignment(g128,g127)
    c: InternalAlignment(g129,g127)
    c: Block(g121)
    c: Block(g127)
    c: Coincident(g130,g121)
    c: Coincident(g130,g127)
    c: Vertical(g130)
    c: Coincident(g131,g127)
    c: Coincident(g131,g64)
    c: Coincident(g132,g64)
    c: Coincident(g132,g121)
    c: Weight(g133) = 1
    c: Equal(g133,g134)
    c: Equal(g133,g135)
    c: InternalAlignment(g133,g136)
    c: InternalAlignment(g134,g136)
    c: InternalAlignment(g135,g136)
    c: InternalAlignment(g137,g136)
    c: InternalAlignment(g138,g136)
    c: Weight(g139) = 1
    c: Equal(g139,g140)
    c: Equal(g139,g141)
    c: InternalAlignment(g139,g142)
    c: InternalAlignment(g140,g142)
    c: InternalAlignment(g141,g142)
    c: InternalAlignment(g143,g142)
    c: InternalAlignment(g144,g142)
    c: Weight(g145) = 1
    c: Equal(g145,g146)
    c: Equal(g145,g147)
    c: InternalAlignment(g145,g148)
    c: InternalAlignment(g146,g148)
    c: InternalAlignment(g147,g148)
    c: InternalAlignment(g149,g148)
    c: InternalAlignment(g150,g148)
    c: Weight(g151) = 1
    c: Equal(g151,g152)
    c: Equal(g151,g153)
    c: InternalAlignment(g151,g154)
    c: InternalAlignment(g152,g154)
    c: InternalAlignment(g153,g154)
    c: InternalAlignment(g155,g154)
    c: InternalAlignment(g156,g154)
    c: Block(g154)
    c: Block(g148)
    c: Block(g142)
    c: Block(g136)
    c: Coincident(g157,g31)
    c: Coincident(g157,g154)
    c: Coincident(g158,g154)
    c: Coincident(g158,g148)
    c: Horizontal(g158)
    c: Coincident(g159,g148)
    c: Coincident(g159,g31)
    c: Vertical(g159)
    c: Coincident(g160,g25)
    c: Coincident(g160,g142)
    c: Vertical(g160)
    c: Coincident(g161,g142)
    c: Coincident(g161,g136)
    c: Horizontal(g161)
    c: Coincident(g162,g136)
    c: Coincident(g162,g25)
    c: Weight(g163) = 1
    c: Equal(g163,g164)
    c: Equal(g163,g165)
    c: InternalAlignment(g163,g166)
    c: InternalAlignment(g164,g166)
    c: InternalAlignment(g165,g166)
    c: InternalAlignment(g167,g166)
    c: InternalAlignment(g168,g166)
    c: Weight(g169) = 1
    c: Equal(g169,g170)
    c: Equal(g169,g171)
    c: InternalAlignment(g169,g172)
    c: InternalAlignment(g170,g172)
    c: InternalAlignment(g171,g172)
    c: InternalAlignment(g173,g172)
    c: InternalAlignment(g174,g172)
    c: Weight(g175) = 1
    c: Equal(g175,g176)
    c: Equal(g175,g177)
    c: InternalAlignment(g175,g178)
    c: InternalAlignment(g176,g178)
    c: InternalAlignment(g177,g178)
    c: InternalAlignment(g179,g178)
    c: InternalAlignment(g180,g178)
    c: Weight(g181) = 1
    c: Equal(g181,g182)
    c: Equal(g181,g183)
    c: InternalAlignment(g181,g184)
    c: InternalAlignment(g182,g184)
    c: InternalAlignment(g183,g184)
    c: InternalAlignment(g185,g184)
    c: InternalAlignment(g186,g184)
    c: Block(g184)
    c: Block(g178)
    c: Block(g172)
    c: Block(g166)
    c: Coincident(g187,g184)
    c: Coincident(g187,g178)
    c: Horizontal(g187)
    c: Coincident(g188,g178)
    c: Coincident(g188,g13)
    c: Vertical(g188)
    c: Coincident(g189,g19)
    c: Coincident(g189,g172)
    c: Vertical(g189)
    c: Coincident(g190,g172)
    c: Coincident(g190,g166)
    c: Horizontal(g190)
    c: Coincident(g191,g166)
    c: Coincident(g191,g19)
    c: Coincident(g192,g13)
    c: Weight(g193) = 1
    c: Equal(g193,g194)
    c: Equal(g193,g195)
    c: InternalAlignment(g193,g196)
    c: InternalAlignment(g194,g196)
    c: InternalAlignment(g195,g196)
    c: InternalAlignment(g197,g196)
    c: InternalAlignment(g198,g196)
    c: Weight(g199) = 1
    c: Equal(g199,g200)
    c: Equal(g199,g201)
    c: InternalAlignment(g199,g202)
    c: InternalAlignment(g200,g202)
    c: InternalAlignment(g201,g202)
    c: InternalAlignment(g203,g202)
    c: InternalAlignment(g204,g202)
    c: Block(g202)
    c: Block(g196)
    c: Coincident(g205,g202)
    c: Coincident(g205,g37)
    c: Coincident(g206,g37)
    c: Coincident(g206,g196)
    c: Coincident(g207,g196)
    c: Coincident(g207,g202)
    c: Vertical(g207)
    c: Weight(g208) = 1
    c: Equal(g208,g209)
    c: Equal(g208,g210)
    c: InternalAlignment(g208,g211)
    c: InternalAlignment(g209,g211)
    c: InternalAlignment(g210,g211)
    c: InternalAlignment(g212,g211)
    c: InternalAlignment(g213,g211)
    c: Weight(g214) = 1
    c: Equal(g214,g215)
    c: Equal(g214,g216)
    c: InternalAlignment(g214,g217)
    c: InternalAlignment(g215,g217)
    c: InternalAlignment(g216,g217)
    c: InternalAlignment(g218,g217)
    c: InternalAlignment(g219,g217)
    c: Block(g217)
    c: Block(g211)
    c: Coincident(g220,g211)
    c: Coincident(g220,g43)
    c: Coincident(g221,g43)
    c: Coincident(g221,g217)
    c: Coincident(g222,g217)
    c: Coincident(g222,g211)
    c: Vertical(g222)
    c: Horizontal(g223)
    c: Block(g223)
    c: Vertical(g224)
    c: Block(g224)
    c: Block(g225)
    c: Weight(g226) = 1
    c: Equal(g226,g227)
    c: Equal(g226,g228)
    c: InternalAlignment(g226,g229)
    c: InternalAlignment(g227,g229)
    c: InternalAlignment(g228,g229)
    c: InternalAlignment(g230,g229)
    c: InternalAlignment(g231,g229)
    c: Weight(g232) = 1
    c: Equal(g232,g233)
    c: Equal(g232,g234)
    c: InternalAlignment(g232,g235)
    c: InternalAlignment(g233,g235)
    c: InternalAlignment(g234,g235)
    c: InternalAlignment(g236,g235)
    c: InternalAlignment(g237,g235)
    c: Weight(g238) = 1
    c: Equal(g238,g239)
    c: Equal(g238,g240)
    c: InternalAlignment(g238,g241)
    c: InternalAlignment(g239,g241)
    c: InternalAlignment(g240,g241)
    c: InternalAlignment(g242,g241)
    c: InternalAlignment(g243,g241)
    c: Weight(g244) = 1
    c: Equal(g244,g245)
    c: Equal(g244,g246)
    c: InternalAlignment(g244,g247)
    c: InternalAlignment(g245,g247)
    c: InternalAlignment(g246,g247)
    c: InternalAlignment(g248,g247)
    c: InternalAlignment(g249,g247)
    c: Block(g229)
    c: Block(g235)
    c: Block(g241)
    c: Block(g247)
    c: Coincident(g250,g235)
    c: Coincident(g250,g229)
    c: Horizontal(g250)
    c: Block(g192)
    c: Weight(g251) = 1
    c: Equal(g251,g252)
    c: Equal(g251,g253)
    c: InternalAlignment(g251,g254)
    c: InternalAlignment(g252,g254)
    c: InternalAlignment(g253,g254)
    c: InternalAlignment(g255,g254)
    c: InternalAlignment(g256,g254)
    c: Weight(g257) = 1
    c: Equal(g257,g258)
    c: Equal(g257,g259)
    c: InternalAlignment(g257,g260)
    c: InternalAlignment(g258,g260)
    c: InternalAlignment(g259,g260)
    c: InternalAlignment(g261,g260)
    c: InternalAlignment(g262,g260)
    c: Block(g254)
    c: Block(g260)
    c: Coincident(g263,g254)
    c: Coincident(g263,g260)
    c: Weight(g264) = 1
    c: Equal(g264,g265)
    c: Equal(g264,g266)
    c: InternalAlignment(g264,g267)
    c: InternalAlignment(g265,g267)
    c: InternalAlignment(g266,g267)
    c: InternalAlignment(g268,g267)
    c: InternalAlignment(g269,g267)
    c: Weight(g270) = 1
    c: Equal(g270,g271)
    c: Equal(g270,g272)
    c: InternalAlignment(g270,g273)
    c: InternalAlignment(g271,g273)
    c: InternalAlignment(g272,g273)
    c: InternalAlignment(g274,g273)
    c: InternalAlignment(g275,g273)
    c: Weight(g276) = 1
    c: Equal(g276,g277)
    c: Equal(g276,g278)
    c: InternalAlignment(g276,g279)
    c: InternalAlignment(g277,g279)
    c: InternalAlignment(g278,g279)
    c: InternalAlignment(g280,g279)
    c: InternalAlignment(g281,g279)
    c: Block(g279)
    c: Block(g273)
    c: Block(g267)
    c: Coincident(g282,g273)
    c: Coincident(g282,g267)
    c: Coincident(g283,g267)
    c: Coincident(g283,g279)
    c: Vertical(g283)
    c: Coincident(g284,g279)
    c: Coincident(g284,g273)
    c: Horizontal(g284)
    c: Weight(g285) = 1
    c: Equal(g285,g286)
    c: InternalAlignment(g285,g287)
    c: InternalAlignment(g286,g287)
    c: InternalAlignment(g288,g287)
    c: InternalAlignment(g289,g287)
    c: Weight(g290) = 1
    c: InternalAlignment(g291,g293)
    c: InternalAlignment(g292,g293)
    c: InternalAlignment(g294,g293)
    c: InternalAlignment(g295,g293)
    c: Weight(g296) = 1
    c: Equal(g296,g297)
    c: Equal(g296,g298)
    c: InternalAlignment(g296,g299)
    c: InternalAlignment(g297,g299)
    c: InternalAlignment(g298,g299)
    c: InternalAlignment(g300,g299)
    c: InternalAlignment(g301,g299)
    c: Equal(g302,g303)
    c: Equal(g302,g304)
    c: InternalAlignment(g302,g305)
    c: InternalAlignment(g303,g305)
    c: InternalAlignment(g304,g305)
    c: InternalAlignment(g306,g305)
    c: InternalAlignment(g307,g305)
    c: Block(g293)
    c: Block(g299)
    c: Block(g305)
    c: Block(g287)
    c: Coincident(g308,g287)
    c: Coincident(g308,g293)
    c: Horizontal(g308)
    c: Coincident(g309,g293)
    c: Coincident(g309,g299)
    c: Vertical(g309)
    c: Coincident(g310,g299)
    c: Coincident(g310,g305)
    c: Horizontal(g310)
    c: Coincident(g311,g305)
    c: Coincident(g311,g287)
    c: Weight(g312) = 1
    c: Equal(g312,g313)
    c: Equal(g312,g314)
    c: InternalAlignment(g312,g315)
    c: InternalAlignment(g313,g315)
    c: InternalAlignment(g314,g315)
    c: InternalAlignment(g316,g315)
    c: InternalAlignment(g317,g315)
    c: Weight(g318) = 1
    c: Equal(g318,g319)
    c: Equal(g318,g320)
    c: InternalAlignment(g318,g321)
    c: InternalAlignment(g319,g321)
    c: InternalAlignment(g320,g321)
    c: InternalAlignment(g322,g321)
    c: InternalAlignment(g323,g321)
    c: Weight(g324) = 1
    c: Equal(g324,g325)
    c: Equal(g324,g326)
    c: InternalAlignment(g324,g327)
    c: InternalAlignment(g325,g327)
    c: InternalAlignment(g326,g327)
    c: InternalAlignment(g328,g327)
    c: InternalAlignment(g329,g327)
    c: Block(g327)
    c: Block(g321)
    c: Block(g315)
    c: Coincident(g330,g327)
    c: Coincident(g330,g321)
    c: Horizontal(g330)
    c: Coincident(g331,g321)
    c: Coincident(g331,g315)
    c: Vertical(g331)
    c: Coincident(g332,g315)
    c: Coincident(g332,g327)
    c: InternalAlignment(g333,g334)
    c: InternalAlignment(g335,g334)
    c: InternalAlignment(g336,g334)
    c: Block(g334)
    c: Equal(g337,g338)
    c: Equal(g337,g339)
    c: InternalAlignment(g337,g340)
    c: InternalAlignment(g338,g340)
    c: InternalAlignment(g339,g340)
    c: InternalAlignment(g341,g340)
    c: InternalAlignment(g342,g340)
    c: Block(g340)
    c: Coincident(g343,g334)
    c: Horizontal(g343)
    c: Block(g343)
    c: Coincident(g344,g334)
    c: Coincident(g344,g260)
    c: Vertical(g344)
    c: Coincident(g345,g340)
    c: Coincident(g345,g254)
    c: Vertical(g345)
    c: Coincident(g347,g5)
    c: Coincident(g348,g5)
    c: Block(g346)
    c: Block(g5)
    c: Block(g348)
    c: Block(g347)
    c: Distance(g344) = 119.89
FEATURE [Sketcher::SketchObject] Sketch001
  FullyConstrained = true
  MapMode = 4
  Placement = pos=(0,0,0) rot=(0.57735,0.57735,0.57735;2.0944rad)
  Support = -> [Sketch]
  sketch-geometry (46):
    g0: BSplineCurve PolesCount=3 KnotsCount=2 Degree=2 IsPeriodic=0
    g1: ArcOfCircle CenterX=73.1223 CenterY=-32.291 CenterZ=0 NormalX=0 NormalY=0 NormalZ=1 AngleXU=0 Radius=13 StartAngle=5.92268 EndAngle=9.06428
    g2: ArcOfCircle CenterX=66.7816 CenterY=-49.1439 CenterZ=0 NormalX=0 NormalY=0 NormalZ=1 AngleXU=0 Radius=13 StartAngle=2.78068 EndAngle=5.92131
    g3: ArcOfCircle CenterX=55.9263 CenterY=-78.1807 CenterZ=0 NormalX=0 NormalY=0 NormalZ=1 AngleXU=0 Radius=13 StartAngle=5.92268 EndAngle=9.06428
    g4: ArcOfCircle CenterX=49.5884 CenterY=-95.0342 CenterZ=0 NormalX=0 NormalY=0 NormalZ=1 AngleXU=0 Radius=13 StartAngle=2.78068 EndAngle=5.92131
    g5: ArcOfCircle CenterX=38.7206 CenterY=-124.067 CenterZ=0 NormalX=0 NormalY=0 NormalZ=1 AngleXU=0 Radius=13 StartAngle=5.92268 EndAngle=9.06428
    g6: ArcOfCircle CenterX=32.3875 CenterY=-140.92 CenterZ=0 NormalX=0 NormalY=0 NormalZ=1 AngleXU=0 Radius=13 StartAngle=2.78068 EndAngle=5.92131
    g7: ArcOfCircle CenterX=21.4715 CenterY=-169.934 CenterZ=0 NormalX=0 NormalY=0 NormalZ=1 AngleXU=0 Radius=13 StartAngle=5.92268 EndAngle=9.06428
    g8: ArcOfCircle CenterX=15.1336 CenterY=-186.787 CenterZ=0 NormalX=0 NormalY=0 NormalZ=1 AngleXU=0 Radius=13 StartAngle=2.78068 EndAngle=5.92131
    g9-g12: Circle x4 (B-spline internal-alignment scaffolding for g13; pole/knot coordinates omitted)
    g13: BSplineCurve PolesCount=4 KnotsCount=2 Degree=3 IsPeriodic=0
    g14: GeomPoint X=28.8094 Y=-19.0875 Z=0
    g15: GeomPoint X=47.0443 Y=-50.4712 Z=0
    g16: Circle CenterX=53.5586 CenterY=-23.2695 CenterZ=0 NormalX=0 NormalY=0 NormalZ=1 AngleXU=0 Radius=3.24518
    g17: Circle CenterX=-195.441 CenterY=-127.082 CenterZ=0 NormalX=0 NormalY=0 NormalZ=1 AngleXU=0 Radius=1
    g18: Circle CenterX=-8.24091 CenterY=-197.481 CenterZ=0 NormalX=0 NormalY=0 NormalZ=1 AngleXU=0 Radius=1
    g19: Circle CenterX=12.8789 CenterY=-141.321 CenterZ=0 NormalX=0 NormalY=0 NormalZ=1 AngleXU=0 Radius=1
    g20: BSplineCurve PolesCount=3 KnotsCount=2 Degree=2 IsPeriodic=0
    g21: GeomPoint X=-195.441 Y=-127.082 Z=0
    g22: GeomPoint X=12.8789 Y=-141.321 Z=0
    g23: Circle CenterX=-12.8016 CenterY=-179.036 CenterZ=0 NormalX=0 NormalY=0 NormalZ=1 AngleXU=0 Radius=10.5072
    g24: Circle CenterX=0.933922 CenterY=-166.43 CenterZ=0 NormalX=0 NormalY=0 NormalZ=1 AngleXU=0 Radius=3.26661
    g25: Circle CenterX=-33.5518 CenterY=-176.44 CenterZ=0 NormalX=0 NormalY=0 NormalZ=1 AngleXU=0 Radius=5.64388
    g26: Circle CenterX=-47.2366 CenterY=-173.859 CenterZ=0 NormalX=0 NormalY=0 NormalZ=1 AngleXU=0 Radius=3.01653
    g27: Circle CenterX=-56.2595 CenterY=-171.456 CenterZ=0 NormalX=0 NormalY=0 NormalZ=1 AngleXU=0 Radius=2.12826
    g28: ArcOfCircle CenterX=51.2151 CenterY=-198.473 CenterZ=0 NormalX=0 NormalY=0 NormalZ=1 AngleXU=0 Radius=20 StartAngle=2.78189 EndAngle=4.35269
    g29: LineSegment StartX=32.4951 StartY=-191.433 StartZ=0 EndX=94.6578 EndY=-26.1352 EndZ=0
    g30: LineSegment StartX=43.1192 StartY=-220.001 StartZ=0 EndX=-196.497 EndY=-129.89 EndZ=0
    g31: LineSegment StartX=43.1192 StartY=-220.001 StartZ=0 EndX=44.1752 EndY=-217.193 EndZ=0
    g32: LineSegment StartX=117.223 StartY=-19.0875 StartZ=0 EndX=117.223 EndY=-16.0875 EndZ=0
    g33: LineSegment StartX=117.223 StartY=-16.0875 StartZ=0 EndX=17.2232 EndY=-16.0875 EndZ=0
    g34: LineSegment StartX=17.2232 StartY=-16.0875 StartZ=0 EndX=17.2232 EndY=-19.0875 EndZ=0
    g35: LineSegment StartX=28.8094 StartY=-19.0875 StartZ=0 EndX=17.2232 EndY=-19.0875 EndZ=0
    g36: LineSegment StartX=47.0443 StartY=-50.4712 StartZ=0 EndX=12.8789 EndY=-141.321 EndZ=0
    g37: LineSegment StartX=-195.441 StartY=-127.082 StartZ=0 EndX=-196.497 EndY=-129.89 EndZ=0
    g38: LineSegment StartX=85.2866 StartY=-36.8766 StartZ=0 EndX=78.9396 EndY=-53.7463 EndZ=0
    g39: LineSegment StartX=60.9579 StartY=-27.7053 StartZ=0 EndX=54.6191 EndY=-44.5532 EndZ=0
    g40: LineSegment StartX=68.0907 StartY=-82.7664 StartZ=0 EndX=61.7465 EndY=-99.6365 EndZ=0
    g41: LineSegment StartX=43.7619 StartY=-73.595 StartZ=0 EndX=37.426 EndY=-90.4435 EndZ=0
    g42: LineSegment StartX=50.885 StartY=-128.652 StartZ=0 EndX=44.5456 EndY=-145.522 EndZ=0
    g43: LineSegment StartX=26.5562 StartY=-119.481 StartZ=0 EndX=20.2251 EndY=-136.329 EndZ=0
    g44: LineSegment StartX=9.3071 StartY=-165.349 StartZ=0 EndX=2.97115 EndY=-182.197 EndZ=0
    g45: LineSegment StartX=33.6358 StartY=-174.52 StartZ=0 EndX=27.2917 EndY=-191.39 EndZ=0
  constraints (71):
    c: Block(g0)
    c: Block(g1)
    c: Block(g2)
    c: Block(g4)
    c: Block(g3)
    c: Block(g6)
    c: Block(g5)
    c: Block(g8)
    c: Block(g7)
    c: Weight(g9) = 1
    c: Equal(g9,g10)
    c: Equal(g9,g11)
    c: Equal(g9,g12)
    c: InternalAlignment(g9-g12 -> g13) x4
    c: InternalAlignment(g14,g13)
    c: InternalAlignment(g15,g13)
    c: Block(g16)
    c: Weight(g17) = 1
    c: Equal(g17,g18)
    c: Equal(g17,g19)
    c: InternalAlignment(g17,g20)
    c: InternalAlignment(g18,g20)
    c: InternalAlignment(g19,g20)
    c: InternalAlignment(g21,g20)
    c: InternalAlignment(g22,g20)
    c: Block(g20)
    c: Block(g23)
    c: Block(g24)
    c: Block(g25)
    c: Block(g26)
    c: Block(g27)
    c: Block(g28)
    c: Coincident(g29,g28)
    c: Coincident(g29,g0)
    c: Block(g13)
    c: Coincident(g31,g30)
    c: Coincident(g31,g28)
    c: Block(g31)
    c: Coincident(g32,g0)
    c: Vertical(g32)
    c: Coincident(g33,g32)
    c: Horizontal(g33)
    c: Coincident(g34,g33)
    c: Vertical(g34)
    c: Block(g33)
    c: Coincident(g35,g13)
    c: Coincident(g35,g34)
    c: Horizontal(g35)
    c: Coincident(g36,g13)
    c: Coincident(g36,g20)
    c: Coincident(g37,g20)
    c: Coincident(g37,g30)
    c: Block(g30)
    c: Coincident(g38,g1)
    c: Coincident(g38,g2)
    c: Coincident(g39,g1)
    c: Coincident(g39,g2)
    c: Coincident(g40,g3)
    c: Coincident(g40,g4)
    c: Coincident(g41,g3)
    c: Coincident(g41,g4)
    c: Coincident(g42,g5)
    c: Coincident(g42,g6)
    c: Coincident(g43,g5)
    c: Coincident(g43,g6)
    c: Coincident(g44,g7)
    c: Coincident(g44,g8)
    c: Coincident(g45,g7)
    c: Coincident(g45,g8)
    c: Distance(g30) = 256
    c: Distance(g33) = 100
FEATURE [Part::Extrusion] Extrude002
  Base = -> Sketch001
  Dir = (1,0,0)
  DirMode = 2
  FaceMakerClass = Part::FaceMakerBullseye
  LengthFwd = 8
  LengthRev = 0
  Solid = true
  Symmetric = false
FEATURE [Sketcher::SketchObject] Sketch002
  FullyConstrained = true
  sketch-geometry (20):
    g0: LineSegment StartX=-2.77179 StartY=-200.304 StartZ=0 EndX=5.22821 EndY=-200.304 EndZ=0
    g1: LineSegment StartX=5.22821 StartY=-200.304 StartZ=0 EndX=5.22821 EndY=-197.304 EndZ=0
    g2: LineSegment StartX=-2.77179 StartY=-200.304 StartZ=0 EndX=-2.77179 EndY=-197.304 EndZ=0
    g3: LineSegment StartX=5.22821 StartY=-197.304 StartZ=0 EndX=8.22821 EndY=-197.304 EndZ=0
    g4: LineSegment StartX=-2.77179 StartY=-197.304 StartZ=0 EndX=-5.77179 EndY=-197.304 EndZ=0
    g5: LineSegment StartX=19.2282 StartY=-203.304 StartZ=0 EndX=19.2282 EndY=-206.304 EndZ=0
    g6: LineSegment StartX=-16.7718 StartY=-203.304 StartZ=0 EndX=-16.7718 EndY=-206.304 EndZ=0
    g7: LineSegment StartX=-16.7718 StartY=-206.304 StartZ=0 EndX=19.2282 EndY=-206.304 EndZ=0
    g8: Circle CenterX=-16.7718 CenterY=-203.304 CenterZ=0 NormalX=0 NormalY=0 NormalZ=1 AngleXU=0 Radius=1
    g9: Circle CenterX=-5.77179 CenterY=-203.304 CenterZ=0 NormalX=0 NormalY=0 NormalZ=1 AngleXU=0 Radius=1
    g10: Circle CenterX=-5.77179 CenterY=-197.304 CenterZ=0 NormalX=0 NormalY=0 NormalZ=1 AngleXU=0 Radius=1
    g11: BSplineCurve PolesCount=3 KnotsCount=2 Degree=2 IsPeriodic=0
    g12: GeomPoint X=-16.7718 Y=-203.304 Z=0
    g13: GeomPoint X=-5.77179 Y=-197.304 Z=0
    g14: Circle CenterX=19.2282 CenterY=-203.304 CenterZ=0 NormalX=0 NormalY=0 NormalZ=1 AngleXU=0 Radius=1
    g15: Circle CenterX=8.22821 CenterY=-203.304 CenterZ=0 NormalX=0 NormalY=0 NormalZ=1 AngleXU=0 Radius=1
    g16: Circle CenterX=8.22821 CenterY=-197.304 CenterZ=0 NormalX=0 NormalY=0 NormalZ=1 AngleXU=0 Radius=1
    g17: BSplineCurve PolesCount=3 KnotsCount=2 Degree=2 IsPeriodic=0
    g18: GeomPoint X=19.2282 Y=-203.304 Z=0
    g19: GeomPoint X=8.22821 Y=-197.304 Z=0
  constraints (41):
    c: Horizontal(g0)
    c: Distance(g0) = 8
    c: Coincident(g1,g0)
    c: Vertical(g1)
    c: Distance(g1) = 3
    c: Coincident(g2,g0)
    c: Vertical(g2)
    c: Distance(g2) = 3
    c: Coincident(g3,g1)
    c: Horizontal(g3)
    c: Distance(g3) = 3
    c: Coincident(g4,g2)
    c: Horizontal(g4)
    c: Distance(g4) = 3
    c: Vertical(g5)
    c: Vertical(g6)
    c: Coincident(g7,g6)
    c: Coincident(g7,g5)
    c: Weight(g8) = 1
    c: Equal(g8,g9)
    c: Equal(g8,g10)
    c: Coincident(g11,g4)
    c: InternalAlignment(g8,g11)
    c: InternalAlignment(g9,g11)
    c: InternalAlignment(g10,g11)
    c: InternalAlignment(g12,g11)
    c: InternalAlignment(g13,g11)
    c: Coincident(g17,g5)
    c: Weight(g14) = 1
    c: Equal(g14,g15)
    c: Equal(g14,g16)
    c: Coincident(g17,g3)
    c: InternalAlignment(g14,g17)
    c: InternalAlignment(g15,g17)
    c: InternalAlignment(g16,g17)
    c: InternalAlignment(g18,g17)
    c: InternalAlignment(g19,g17)
    c: Block(g7)
    c: Block(g17)
    c: Block(g11)
    c: Block(g6)
FEATURE [Part::Extrusion] Extrude003
  Base = -> Sketch002
  Dir = (0,0,1)
  DirMode = 2
  FaceMakerClass = Part::FaceMakerBullseye
  LengthFwd = 260
  LengthRev = 0
  Solid = true
  Symmetric = false
FEATURE [Sketcher::SketchObject] Sketch003
  FullyConstrained = false
  sketch-geometry (397):
    g0: LineSegment StartX=-42.9272 StartY=136.221 StartZ=0 EndX=-42.9272 EndY=-103.779 EndZ=0
    g1: LineSegment StartX=407.073 StartY=136.221 StartZ=0 EndX=407.073 EndY=-103.779 EndZ=0
    g2: ArcOfCircle CenterX=-26.9272 CenterY=-83.7794 CenterZ=0 NormalX=0 NormalY=0 NormalZ=1 AngleXU=0 Radius=8 StartAngle=3.14159 EndAngle=6.28319
    g3: ArcOfCircle CenterX=391.073 CenterY=-83.7794 CenterZ=0 NormalX=0 NormalY=0 NormalZ=1 AngleXU=0 Radius=8 StartAngle=3.14159 EndAngle=6.28319
    g4: Circle CenterX=175.022 CenterY=27.0628 CenterZ=0 NormalX=0 NormalY=0 NormalZ=1 AngleXU=0 Radius=1
    g5: Circle CenterX=179.022 CenterY=24.8665 CenterZ=0 NormalX=0 NormalY=0 NormalZ=1 AngleXU=0 Radius=1
    g6: Circle CenterX=179.022 CenterY=27.0628 CenterZ=0 NormalX=0 NormalY=0 NormalZ=1 AngleXU=0 Radius=1
    g7: BSplineCurve PolesCount=3 KnotsCount=2 Degree=2 IsPeriodic=0
    g8: GeomPoint X=175.022 Y=27.0628 Z=0
    g9: GeomPoint X=179.022 Y=27.0628 Z=0
    g10: Circle CenterX=189.124 CenterY=27.0628 CenterZ=0 NormalX=0 NormalY=0 NormalZ=1 AngleXU=0 Radius=1
    g11: Circle CenterX=185.124 CenterY=24.8665 CenterZ=0 NormalX=0 NormalY=0 NormalZ=1 AngleXU=0 Radius=1
    g12: Circle CenterX=185.124 CenterY=27.0628 CenterZ=0 NormalX=0 NormalY=0 NormalZ=1 AngleXU=0 Radius=1
    g13: BSplineCurve PolesCount=3 KnotsCount=2 Degree=2 IsPeriodic=0
    g14: GeomPoint X=189.124 Y=27.0628 Z=0
    g15: GeomPoint X=185.124 Y=27.0628 Z=0
    g16: Circle CenterX=175.022 CenterY=5.37834 CenterZ=0 NormalX=0 NormalY=0 NormalZ=1 AngleXU=0 Radius=1
    g17: Circle CenterX=179.022 CenterY=7.57463 CenterZ=0 NormalX=0 NormalY=0 NormalZ=1 AngleXU=0 Radius=1
    g18: Circle CenterX=179.022 CenterY=5.34704 CenterZ=0 NormalX=0 NormalY=0 NormalZ=1 AngleXU=0 Radius=1
    g19: BSplineCurve PolesCount=3 KnotsCount=2 Degree=2 IsPeriodic=0
    g20: GeomPoint X=175.022 Y=5.37834 Z=0
    g21: GeomPoint X=179.022 Y=5.34704 Z=0
    g22: Circle CenterX=189.124 CenterY=5.37834 CenterZ=0 NormalX=0 NormalY=0 NormalZ=1 AngleXU=0 Radius=1
    g23: Circle CenterX=185.124 CenterY=7.57463 CenterZ=0 NormalX=0 NormalY=0 NormalZ=1 AngleXU=0 Radius=1
    g24: Circle CenterX=185.124 CenterY=5.34704 CenterZ=0 NormalX=0 NormalY=0 NormalZ=1 AngleXU=0 Radius=1
    g25: BSplineCurve PolesCount=3 KnotsCount=2 Degree=2 IsPeriodic=0
    g26: GeomPoint X=189.124 Y=5.37834 Z=0
    g27: GeomPoint X=185.124 Y=5.34704 Z=0
    g28: Circle CenterX=165.871 CenterY=18.1458 CenterZ=0 NormalX=0 NormalY=0 NormalZ=1 AngleXU=0 Radius=1
    g29: Circle CenterX=169.377 CenterY=16.2206 CenterZ=0 NormalX=0 NormalY=0 NormalZ=1 AngleXU=0 Radius=1
    g30: Circle CenterX=165.871 CenterY=14.2954 CenterZ=0 NormalX=0 NormalY=0 NormalZ=1 AngleXU=0 Radius=1
    g31: BSplineCurve PolesCount=3 KnotsCount=2 Degree=2 IsPeriodic=0
    g32: GeomPoint X=165.871 Y=18.1458 Z=0
    g33: GeomPoint X=165.871 Y=14.2954 Z=0
    g34: Circle CenterX=198.275 CenterY=18.1458 CenterZ=0 NormalX=0 NormalY=0 NormalZ=1 AngleXU=0 Radius=1
    g35: Circle CenterX=194.768 CenterY=16.2206 CenterZ=0 NormalX=0 NormalY=0 NormalZ=1 AngleXU=0 Radius=1
    g36: Circle CenterX=198.275 CenterY=14.2954 CenterZ=0 NormalX=0 NormalY=0 NormalZ=1 AngleXU=0 Radius=1
    g37: BSplineCurve PolesCount=3 KnotsCount=2 Degree=2 IsPeriodic=0
    g38: GeomPoint X=198.275 Y=18.1458 Z=0
    g39: GeomPoint X=198.275 Y=14.2954 Z=0
    g40: LineSegment StartX=407.073 StartY=-103.779 StartZ=0 EndX=-42.9272 EndY=-103.779 EndZ=0
    g41: Circle CenterX=125.607 CenterY=54.1951 CenterZ=0 NormalX=0 NormalY=0 NormalZ=1 AngleXU=0 Radius=1
    g42: Circle CenterX=139.632 CenterY=46.4944 CenterZ=0 NormalX=0 NormalY=0 NormalZ=1 AngleXU=0 Radius=1
    g43: Circle CenterX=127.326 CenterY=56.7187 CenterZ=0 NormalX=0 NormalY=0 NormalZ=1 AngleXU=0 Radius=1
    g44: BSplineCurve PolesCount=3 KnotsCount=2 Degree=2 IsPeriodic=0
    g45: GeomPoint X=125.607 Y=54.1951 Z=0
    g46: GeomPoint X=127.326 Y=56.7187 Z=0
    g47: Circle CenterX=236.821 CenterY=56.7187 CenterZ=0 NormalX=0 NormalY=0 NormalZ=1 AngleXU=0 Radius=1
    g48: Circle CenterX=224.513 CenterY=46.4944 CenterZ=0 NormalX=0 NormalY=0 NormalZ=1 AngleXU=0 Radius=1
    g49: Circle CenterX=238.538 CenterY=54.1951 CenterZ=0 NormalX=0 NormalY=0 NormalZ=1 AngleXU=0 Radius=1
    g50: BSplineCurve PolesCount=3 KnotsCount=2 Degree=2 IsPeriodic=0
    g51: GeomPoint X=236.821 Y=56.7187 Z=0
    g52: GeomPoint X=238.538 Y=54.1951 Z=0
    g53: Circle CenterX=238.538 CenterY=-21.7539 CenterZ=0 NormalX=0 NormalY=0 NormalZ=1 AngleXU=0 Radius=1
    g54: Circle CenterX=224.513 CenterY=-14.0532 CenterZ=0 NormalX=0 NormalY=0 NormalZ=1 AngleXU=0 Radius=1
    g55: Circle CenterX=236.821 CenterY=-24.2775 CenterZ=0 NormalX=0 NormalY=0 NormalZ=1 AngleXU=0 Radius=1
    g56: BSplineCurve PolesCount=3 KnotsCount=2 Degree=2 IsPeriodic=0
    g57: GeomPoint X=238.538 Y=-21.7539 Z=0
    g58: GeomPoint X=236.821 Y=-24.2775 Z=0
    g59: Circle CenterX=125.607 CenterY=-21.7539 CenterZ=0 NormalX=0 NormalY=0 NormalZ=1 AngleXU=0 Radius=1
    g60: Circle CenterX=139.632 CenterY=-14.0532 CenterZ=0 NormalX=0 NormalY=0 NormalZ=1 AngleXU=0 Radius=1
    g61: Circle CenterX=127.325 CenterY=-24.2775 CenterZ=0 NormalX=0 NormalY=0 NormalZ=1 AngleXU=0 Radius=1
    g62: BSplineCurve PolesCount=3 KnotsCount=2 Degree=2 IsPeriodic=0
    g63: GeomPoint X=125.607 Y=-21.7539 Z=0
    g64: GeomPoint X=127.325 Y=-24.2775 Z=0
    g65: Circle CenterX=302.996 CenterY=111.695 CenterZ=0 NormalX=0 NormalY=0 NormalZ=1 AngleXU=0 Radius=1
    g66: Circle CenterX=306.073 CenterY=114.251 CenterZ=0 NormalX=0 NormalY=0 NormalZ=1 AngleXU=0 Radius=1
    g67: Circle CenterX=306.073 CenterY=110.251 CenterZ=0 NormalX=0 NormalY=0 NormalZ=1 AngleXU=0 Radius=1
    g68: BSplineCurve PolesCount=3 KnotsCount=2 Degree=2 IsPeriodic=0
    g69: GeomPoint X=302.996 Y=111.695 Z=0
    g70: GeomPoint X=306.073 Y=110.251 Z=0
    g71: Circle CenterX=306.073 CenterY=95.2763 CenterZ=0 NormalX=0 NormalY=0 NormalZ=1 AngleXU=0 Radius=1
    g72: Circle CenterX=306.073 CenterY=91.2763 CenterZ=0 NormalX=0 NormalY=0 NormalZ=1 AngleXU=0 Radius=1
    g73: Circle CenterX=302.567 CenterY=89.3511 CenterZ=0 NormalX=0 NormalY=0 NormalZ=1 AngleXU=0 Radius=1
    g74: BSplineCurve PolesCount=3 KnotsCount=2 Degree=2 IsPeriodic=0
    g75: GeomPoint X=306.073 Y=95.2763 Z=0
    g76: GeomPoint X=302.567 Y=89.3511 Z=0
    g77: LineSegment StartX=306.073 StartY=110.251 StartZ=0 EndX=306.073 EndY=95.2763 EndZ=0
    g78: LineSegment StartX=302.996 StartY=111.695 StartZ=0 EndX=236.821 EndY=56.7187 EndZ=0
    g79: LineSegment StartX=238.538 StartY=54.1951 StartZ=0 EndX=302.567 EndY=89.3511 EndZ=0
    g80: Circle CenterX=61.1496 CenterY=111.695 CenterZ=0 NormalX=0 NormalY=0 NormalZ=1 AngleXU=0 Radius=1
    g81: Circle CenterX=58.0728 CenterY=114.251 CenterZ=0 NormalX=0 NormalY=0 NormalZ=1 AngleXU=0 Radius=1
    g82: Circle CenterX=58.0728 CenterY=110.251 CenterZ=0 NormalX=0 NormalY=0 NormalZ=1 AngleXU=0 Radius=1
    g83: BSplineCurve PolesCount=3 KnotsCount=2 Degree=2 IsPeriodic=0
    g84: GeomPoint X=61.1496 Y=111.695 Z=0
    g85: GeomPoint X=58.0728 Y=110.251 Z=0
    g86: Circle CenterX=61.5791 CenterY=89.3511 CenterZ=0 NormalX=0 NormalY=0 NormalZ=1 AngleXU=0 Radius=1
    g87: Circle CenterX=58.0728 CenterY=91.2763 CenterZ=0 NormalX=0 NormalY=0 NormalZ=1 AngleXU=0 Radius=1
    g88: Circle CenterX=58.0728 CenterY=95.2763 CenterZ=0 NormalX=0 NormalY=0 NormalZ=1 AngleXU=0 Radius=1
    g89: BSplineCurve PolesCount=3 KnotsCount=2 Degree=2 IsPeriodic=0
    g90: GeomPoint X=61.5791 Y=89.3511 Z=0
    g91: GeomPoint X=58.0728 Y=95.2763 Z=0
    g92: LineSegment StartX=58.0728 StartY=110.251 StartZ=0 EndX=58.0728 EndY=95.2763 EndZ=0
    g93: LineSegment StartX=61.1496 StartY=111.695 StartZ=0 EndX=127.326 EndY=56.7187 EndZ=0
    g94: LineSegment StartX=125.607 StartY=54.1951 StartZ=0 EndX=61.5791 EndY=89.3511 EndZ=0
    g95: Circle CenterX=61.5791 CenterY=-56.9099 CenterZ=0 NormalX=0 NormalY=0 NormalZ=1 AngleXU=0 Radius=1
    g96: Circle CenterX=58.0728 CenterY=-58.8351 CenterZ=0 NormalX=0 NormalY=0 NormalZ=1 AngleXU=0 Radius=1
    g97: Circle CenterX=58.0728 CenterY=-62.8351 CenterZ=0 NormalX=0 NormalY=0 NormalZ=1 AngleXU=0 Radius=1
    g98: BSplineCurve PolesCount=3 KnotsCount=2 Degree=2 IsPeriodic=0
    g99: GeomPoint X=61.5791 Y=-56.9099 Z=0
    g100: GeomPoint X=58.0728 Y=-62.8351 Z=0
    g101: Circle CenterX=58.0728 CenterY=-77.8102 CenterZ=0 NormalX=0 NormalY=0 NormalZ=1 AngleXU=0 Radius=1
    g102: Circle CenterX=58.0728 CenterY=-81.8102 CenterZ=0 NormalX=0 NormalY=0 NormalZ=1 AngleXU=0 Radius=1
    g103: Circle CenterX=61.1496 CenterY=-79.2541 CenterZ=0 NormalX=0 NormalY=0 NormalZ=1 AngleXU=0 Radius=1
    g104: BSplineCurve PolesCount=3 KnotsCount=2 Degree=2 IsPeriodic=0
    g105: GeomPoint X=58.0728 Y=-77.8102 Z=0
    g106: GeomPoint X=61.1496 Y=-79.2541 Z=0
    g107: LineSegment StartX=58.0728 StartY=-62.8351 StartZ=0 EndX=58.0728 EndY=-77.8102 EndZ=0
    g108: LineSegment StartX=61.1496 StartY=-79.2541 StartZ=0 EndX=127.325 EndY=-24.2775 EndZ=0
    g109: LineSegment StartX=125.607 StartY=-21.7539 StartZ=0 EndX=61.5791 EndY=-56.9099 EndZ=0
    g110: Circle CenterX=302.567 CenterY=-56.9099 CenterZ=0 NormalX=0 NormalY=0 NormalZ=1 AngleXU=0 Radius=1
    g111: Circle CenterX=306.073 CenterY=-58.8351 CenterZ=0 NormalX=0 NormalY=0 NormalZ=1 AngleXU=0 Radius=1
    g112: Circle CenterX=306.073 CenterY=-62.8351 CenterZ=0 NormalX=0 NormalY=0 NormalZ=1 AngleXU=0 Radius=1
    g113: BSplineCurve PolesCount=3 KnotsCount=2 Degree=2 IsPeriodic=0
    g114: GeomPoint X=302.567 Y=-56.9099 Z=0
    g115: GeomPoint X=306.073 Y=-62.8351 Z=0
    g116: Circle CenterX=302.996 CenterY=-79.2541 CenterZ=0 NormalX=0 NormalY=0 NormalZ=1 AngleXU=0 Radius=1
    g117: Circle CenterX=306.073 CenterY=-81.8102 CenterZ=0 NormalX=0 NormalY=0 NormalZ=1 AngleXU=0 Radius=1
    g118: Circle CenterX=306.073 CenterY=-77.8102 CenterZ=0 NormalX=0 NormalY=0 NormalZ=1 AngleXU=0 Radius=1
    g119: BSplineCurve PolesCount=3 KnotsCount=2 Degree=2 IsPeriodic=0
    g120: GeomPoint X=302.996 Y=-79.2541 Z=0
    g121: GeomPoint X=306.073 Y=-77.8102 Z=0
    g122: LineSegment StartX=306.073 StartY=-62.8351 StartZ=0 EndX=306.073 EndY=-77.8102 EndZ=0
    g123: LineSegment StartX=302.996 StartY=-79.2541 StartZ=0 EndX=236.821 EndY=-24.2775 EndZ=0
    g124: LineSegment StartX=238.538 StartY=-21.7539 StartZ=0 EndX=302.567 EndY=-56.9099 EndZ=0
    g125: Circle CenterX=61.6457 CenterY=-88.8112 CenterZ=0 NormalX=0 NormalY=0 NormalZ=1 AngleXU=0 Radius=1
    g126: Circle CenterX=58.0728 CenterY=-91.7794 CenterZ=0 NormalX=0 NormalY=0 NormalZ=1 AngleXU=0 Radius=1
    g127: Circle CenterX=63.9135 CenterY=-91.7794 CenterZ=0 NormalX=0 NormalY=0 NormalZ=1 AngleXU=0 Radius=1
    g128: BSplineCurve PolesCount=3 KnotsCount=2 Degree=2 IsPeriodic=0
    g129: GeomPoint X=61.6457 Y=-88.8112 Z=0
    g130: GeomPoint X=63.9135 Y=-91.7794 Z=0
    g131: Circle CenterX=179.022 CenterY=-85.8163 CenterZ=0 NormalX=0 NormalY=0 NormalZ=1 AngleXU=0 Radius=1
    g132: Circle CenterX=179.022 CenterY=-91.7794 CenterZ=0 NormalX=0 NormalY=0 NormalZ=1 AngleXU=0 Radius=1
    g133: Circle CenterX=171.895 CenterY=-91.7794 CenterZ=0 NormalX=0 NormalY=0 NormalZ=1 AngleXU=0 Radius=1
    g134: BSplineCurve PolesCount=3 KnotsCount=2 Degree=2 IsPeriodic=0
    g135: GeomPoint X=179.022 Y=-85.8163 Z=0
    g136: GeomPoint X=171.895 Y=-91.7794 Z=0
    g137: Circle CenterX=185.124 CenterY=-86.2028 CenterZ=0 NormalX=0 NormalY=0 NormalZ=1 AngleXU=0 Radius=1
    g138: Circle CenterX=185.124 CenterY=-91.7794 CenterZ=0 NormalX=0 NormalY=0 NormalZ=1 AngleXU=0 Radius=1
    g139: Circle CenterX=191.747 CenterY=-91.7794 CenterZ=0 NormalX=0 NormalY=0 NormalZ=1 AngleXU=0 Radius=1
    g140: BSplineCurve PolesCount=3 KnotsCount=2 Degree=2 IsPeriodic=0
    g141: GeomPoint X=185.124 Y=-86.2028 Z=0
    g142: GeomPoint X=191.747 Y=-91.7794 Z=0
    g143: Circle CenterX=299.888 CenterY=-86.6413 CenterZ=0 NormalX=0 NormalY=0 NormalZ=1 AngleXU=0 Radius=1
    g144: Circle CenterX=306.073 CenterY=-91.7794 CenterZ=0 NormalX=0 NormalY=0 NormalZ=1 AngleXU=0 Radius=1
    g145: Circle CenterX=298.776 CenterY=-91.7794 CenterZ=0 NormalX=0 NormalY=0 NormalZ=1 AngleXU=0 Radius=1
    g146: BSplineCurve PolesCount=3 KnotsCount=2 Degree=2 IsPeriodic=0
    g147: GeomPoint X=299.888 Y=-86.6413 Z=0
    g148: GeomPoint X=298.776 Y=-91.7794 Z=0
    g149: LineSegment StartX=189.124 StartY=5.37834 StartZ=0 EndX=299.888 EndY=-86.6413 EndZ=0
    g150: LineSegment StartX=298.776 StartY=-91.7794 StartZ=0 EndX=191.747 EndY=-91.7794 EndZ=0
    g151: LineSegment StartX=185.124 StartY=-86.2028 StartZ=0 EndX=185.124 EndY=5.34704 EndZ=0
    g152: LineSegment StartX=179.022 StartY=5.34704 StartZ=0 EndX=179.022 EndY=-85.8163 EndZ=0
    g153: LineSegment StartX=171.895 StartY=-91.7794 StartZ=0 EndX=63.9135 EndY=-91.7794 EndZ=0
    g154: LineSegment StartX=61.6457 StartY=-88.8112 StartZ=0 EndX=175.022 EndY=5.37834 EndZ=0
    g155: Circle CenterX=302.073 CenterY=124.221 CenterZ=0 NormalX=0 NormalY=0 NormalZ=1 AngleXU=0 Radius=1
    g156: Circle CenterX=306.073 CenterY=124.221 CenterZ=0 NormalX=0 NormalY=0 NormalZ=1 AngleXU=0 Radius=1
    g157: Circle CenterX=302.996 CenterY=121.665 CenterZ=0 NormalX=0 NormalY=0 NormalZ=1 AngleXU=0 Radius=1
    g158: BSplineCurve PolesCount=3 KnotsCount=2 Degree=2 IsPeriodic=0
    g159: GeomPoint X=302.073 Y=124.221 Z=0
    g160: GeomPoint X=302.996 Y=121.665 Z=0
    g161: Circle CenterX=189.124 CenterY=124.221 CenterZ=0 NormalX=0 NormalY=0 NormalZ=1 AngleXU=0 Radius=1
    g162: Circle CenterX=185.124 CenterY=124.221 CenterZ=0 NormalX=0 NormalY=0 NormalZ=1 AngleXU=0 Radius=1
    g163: Circle CenterX=185.124 CenterY=120.221 CenterZ=0 NormalX=0 NormalY=0 NormalZ=1 AngleXU=0 Radius=1
    g164: BSplineCurve PolesCount=3 KnotsCount=2 Degree=2 IsPeriodic=0
    g165: GeomPoint X=189.124 Y=124.221 Z=0
    g166: GeomPoint X=185.124 Y=120.221 Z=0
    g167: Circle CenterX=175.022 CenterY=124.221 CenterZ=0 NormalX=0 NormalY=0 NormalZ=1 AngleXU=0 Radius=1
    g168: Circle CenterX=179.022 CenterY=124.221 CenterZ=0 NormalX=0 NormalY=0 NormalZ=1 AngleXU=0 Radius=1
    g169: Circle CenterX=179.022 CenterY=120.221 CenterZ=0 NormalX=0 NormalY=0 NormalZ=1 AngleXU=0 Radius=1
    g170: BSplineCurve PolesCount=3 KnotsCount=2 Degree=2 IsPeriodic=0
    g171: GeomPoint X=175.022 Y=124.221 Z=0
    g172: GeomPoint X=179.022 Y=120.221 Z=0
    g173: Circle CenterX=62.0728 CenterY=124.221 CenterZ=0 NormalX=0 NormalY=0 NormalZ=1 AngleXU=0 Radius=1
    g174: Circle CenterX=58.0728 CenterY=124.221 CenterZ=0 NormalX=0 NormalY=0 NormalZ=1 AngleXU=0 Radius=1
    g175: Circle CenterX=61.1496 CenterY=121.665 CenterZ=0 NormalX=0 NormalY=0 NormalZ=1 AngleXU=0 Radius=1
    g176: BSplineCurve PolesCount=3 KnotsCount=2 Degree=2 IsPeriodic=0
    g177: GeomPoint X=62.0728 Y=124.221 Z=0
    g178: GeomPoint X=61.1496 Y=121.665 Z=0
    g179: LineSegment StartX=179.022 StartY=120.221 StartZ=0 EndX=179.022 EndY=27.0628 EndZ=0
    g180: LineSegment StartX=185.124 StartY=27.0628 StartZ=0 EndX=185.124 EndY=120.221 EndZ=0
    g181: LineSegment StartX=302.996 StartY=121.665 StartZ=0 EndX=189.124 EndY=27.0628 EndZ=0
    g182: LineSegment StartX=175.022 StartY=27.0628 StartZ=0 EndX=61.1496 EndY=121.665 EndZ=0
    g183: Circle CenterX=61.5791 CenterY=75.4095 CenterZ=0 NormalX=0 NormalY=0 NormalZ=1 AngleXU=0 Radius=1
    g184: Circle CenterX=58.0728 CenterY=77.3346 CenterZ=0 NormalX=0 NormalY=0 NormalZ=1 AngleXU=0 Radius=1
    g185: Circle CenterX=58.0728 CenterY=73.3346 CenterZ=0 NormalX=0 NormalY=0 NormalZ=1 AngleXU=0 Radius=1
    g186: BSplineCurve PolesCount=3 KnotsCount=2 Degree=2 IsPeriodic=0
    g187: GeomPoint X=61.5791 Y=75.4095 Z=0
    g188: GeomPoint X=58.0728 Y=73.3346 Z=0
    g189: Circle CenterX=58.0728 CenterY=-40.8935 CenterZ=0 NormalX=0 NormalY=0 NormalZ=1 AngleXU=0 Radius=1
    g190: Circle CenterX=58.0728 CenterY=-44.8935 CenterZ=0 NormalX=0 NormalY=0 NormalZ=1 AngleXU=0 Radius=1
    g191: Circle CenterX=61.5791 CenterY=-42.9683 CenterZ=0 NormalX=0 NormalY=0 NormalZ=1 AngleXU=0 Radius=1
    g192: BSplineCurve PolesCount=3 KnotsCount=2 Degree=2 IsPeriodic=0
    g193: GeomPoint X=58.0728 Y=-40.8935 Z=0
    g194: GeomPoint X=61.5791 Y=-42.9683 Z=0
    g195: LineSegment StartX=61.5791 StartY=-42.9683 StartZ=0 EndX=165.871 EndY=14.2954 EndZ=0
    g196: LineSegment StartX=165.871 StartY=18.1458 StartZ=0 EndX=61.5791 EndY=75.4095 EndZ=0
    g197: LineSegment StartX=58.0728 StartY=73.3346 StartZ=0 EndX=58.0728 EndY=-40.8935 EndZ=0
    g198: Circle CenterX=302.567 CenterY=-42.9683 CenterZ=0 NormalX=0 NormalY=0 NormalZ=1 AngleXU=0 Radius=1
    g199: Circle CenterX=306.073 CenterY=-44.8935 CenterZ=0 NormalX=0 NormalY=0 NormalZ=1 AngleXU=0 Radius=1
    g200: Circle CenterX=306.073 CenterY=-40.8935 CenterZ=0 NormalX=0 NormalY=0 NormalZ=1 AngleXU=0 Radius=1
    g201: BSplineCurve PolesCount=3 KnotsCount=2 Degree=2 IsPeriodic=0
    g202: GeomPoint X=302.567 Y=-42.9683 Z=0
    g203: GeomPoint X=306.073 Y=-40.8935 Z=0
    g204: Circle CenterX=306.073 CenterY=73.3346 CenterZ=0 NormalX=0 NormalY=0 NormalZ=1 AngleXU=0 Radius=1
    g205: Circle CenterX=306.073 CenterY=77.3346 CenterZ=0 NormalX=0 NormalY=0 NormalZ=1 AngleXU=0 Radius=1
    g206: Circle CenterX=302.567 CenterY=75.4095 CenterZ=0 NormalX=0 NormalY=0 NormalZ=1 AngleXU=0 Radius=1
    g207: BSplineCurve PolesCount=3 KnotsCount=2 Degree=2 IsPeriodic=0
    g208: GeomPoint X=306.073 Y=73.3346 Z=0
    g209: GeomPoint X=302.567 Y=75.4095 Z=0
    g210: LineSegment StartX=302.567 StartY=-42.9683 StartZ=0 EndX=198.275 EndY=14.2954 EndZ=0
    g211: LineSegment StartX=198.275 StartY=18.1458 StartZ=0 EndX=302.567 EndY=75.4095 EndZ=0
    g212: LineSegment StartX=306.073 StartY=73.3346 StartZ=0 EndX=306.073 EndY=-40.8935 EndZ=0
    g213: LineSegment StartX=322.073 StartY=105.865 StartZ=0 EndX=328.643 EndY=105.865 EndZ=0
    g214: LineSegment StartX=318.073 StartY=120.221 StartZ=0 EndX=318.073 EndY=109.865 EndZ=0
    g215: LineSegment StartX=336.157 StartY=107.779 StartZ=0 EndX=362.567 EndY=122.294 EndZ=0
    g216: Circle CenterX=362.073 CenterY=124.221 CenterZ=0 NormalX=0 NormalY=0 NormalZ=1 AngleXU=0 Radius=1
    g217: Circle CenterX=366.073 CenterY=124.221 CenterZ=0 NormalX=0 NormalY=0 NormalZ=1 AngleXU=0 Radius=1
    g218: Circle CenterX=362.567 CenterY=122.294 CenterZ=0 NormalX=0 NormalY=0 NormalZ=1 AngleXU=0 Radius=1
    g219: BSplineCurve PolesCount=3 KnotsCount=2 Degree=2 IsPeriodic=0
    g220: GeomPoint X=362.073 Y=124.221 Z=0
    g221: GeomPoint X=362.567 Y=122.294 Z=0
    g222: Circle CenterX=322.073 CenterY=124.221 CenterZ=0 NormalX=0 NormalY=0 NormalZ=1 AngleXU=0 Radius=1
    g223: Circle CenterX=318.073 CenterY=124.221 CenterZ=0 NormalX=0 NormalY=0 NormalZ=1 AngleXU=0 Radius=1
    g224: Circle CenterX=318.073 CenterY=120.221 CenterZ=0 NormalX=0 NormalY=0 NormalZ=1 AngleXU=0 Radius=1
    g225: BSplineCurve PolesCount=3 KnotsCount=2 Degree=2 IsPeriodic=0
    g226: GeomPoint X=322.073 Y=124.221 Z=0
    g227: GeomPoint X=318.073 Y=120.221 Z=0
    g228: Circle CenterX=322.073 CenterY=105.865 CenterZ=0 NormalX=0 NormalY=0 NormalZ=1 AngleXU=0 Radius=1
    g229: Circle CenterX=318.073 CenterY=105.865 CenterZ=0 NormalX=0 NormalY=0 NormalZ=1 AngleXU=0 Radius=1
    g230: Circle CenterX=318.073 CenterY=109.865 CenterZ=0 NormalX=0 NormalY=0 NormalZ=1 AngleXU=0 Radius=1
    g231: BSplineCurve PolesCount=3 KnotsCount=2 Degree=2 IsPeriodic=0
    g232: GeomPoint X=322.073 Y=105.865 Z=0
    g233: GeomPoint X=318.073 Y=109.865 Z=0
    g234: Circle CenterX=336.157 CenterY=107.779 CenterZ=0 NormalX=0 NormalY=0 NormalZ=1 AngleXU=0 Radius=1
    g235: Circle CenterX=332.651 CenterY=105.853 CenterZ=0 NormalX=0 NormalY=0 NormalZ=1 AngleXU=0 Radius=1
    g236: Circle CenterX=328.643 CenterY=105.865 CenterZ=0 NormalX=0 NormalY=0 NormalZ=1 AngleXU=0 Radius=1
    g237: BSplineCurve PolesCount=3 KnotsCount=2 Degree=2 IsPeriodic=0
    g238: GeomPoint X=336.157 Y=107.779 Z=0
    g239: GeomPoint X=328.643 Y=105.865 Z=0
    g240: LineSegment StartX=322.073 StartY=124.221 StartZ=0 EndX=362.073 EndY=124.221 EndZ=0
    g241: Circle CenterX=371.567 CenterY=-80.8644 CenterZ=0 NormalX=0 NormalY=0 NormalZ=1 AngleXU=0 Radius=1
    g242: Circle CenterX=375.073 CenterY=-82.7896 CenterZ=0 NormalX=0 NormalY=0 NormalZ=1 AngleXU=0 Radius=1
    g243: Circle CenterX=375.073 CenterY=-78.7896 CenterZ=0 NormalX=0 NormalY=0 NormalZ=1 AngleXU=0 Radius=1
    g244: BSplineCurve PolesCount=3 KnotsCount=2 Degree=2 IsPeriodic=0
    g245: GeomPoint X=371.567 Y=-80.8644 Z=0
    g246: GeomPoint X=375.073 Y=-78.7896 Z=0
    g247: Circle CenterX=321.579 CenterY=-53.4075 CenterZ=0 NormalX=0 NormalY=0 NormalZ=1 AngleXU=0 Radius=1
    g248: Circle CenterX=318.073 CenterY=-51.4823 CenterZ=0 NormalX=0 NormalY=0 NormalZ=1 AngleXU=0 Radius=1
    g249: Circle CenterX=318.073 CenterY=-47.4805 CenterZ=0 NormalX=0 NormalY=0 NormalZ=1 AngleXU=0 Radius=1
    g250: BSplineCurve PolesCount=3 KnotsCount=2 Degree=2 IsPeriodic=0
    g251: GeomPoint X=321.579 Y=-53.4075 Z=0
    g252: GeomPoint X=318.073 Y=-47.4805 Z=0
    g253: LineSegment StartX=371.567 StartY=-80.8644 StartZ=0 EndX=321.579 EndY=-53.4075 EndZ=0
    g254: Circle CenterX=321.579 CenterY=-67.3492 CenterZ=0 NormalX=0 NormalY=0 NormalZ=1 AngleXU=0 Radius=1
    g255: Circle CenterX=318.073 CenterY=-65.424 CenterZ=0 NormalX=0 NormalY=0 NormalZ=1 AngleXU=0 Radius=1
    g256: Circle CenterX=318.073 CenterY=-69.424 CenterZ=0 NormalX=0 NormalY=0 NormalZ=1 AngleXU=0 Radius=1
    g257: BSplineCurve PolesCount=3 KnotsCount=2 Degree=2 IsPeriodic=0
    g258: GeomPoint X=321.579 Y=-67.3492 Z=0
    g259: GeomPoint X=318.073 Y=-69.424 Z=0
    g260: Circle CenterX=362.567 CenterY=-89.8542 CenterZ=0 NormalX=0 NormalY=0 NormalZ=1 AngleXU=0 Radius=1
    g261: Circle CenterX=366.073 CenterY=-91.7794 CenterZ=0 NormalX=0 NormalY=0 NormalZ=1 AngleXU=0 Radius=1
    g262: Circle CenterX=362.073 CenterY=-91.7794 CenterZ=0 NormalX=0 NormalY=0 NormalZ=1 AngleXU=0 Radius=1
    g263: BSplineCurve PolesCount=3 KnotsCount=2 Degree=2 IsPeriodic=0
    g264: GeomPoint X=362.567 Y=-89.8542 Z=0
    g265: GeomPoint X=362.073 Y=-91.7794 Z=0
    g266: Circle CenterX=322.073 CenterY=-91.7794 CenterZ=0 NormalX=0 NormalY=0 NormalZ=1 AngleXU=0 Radius=1
    g267: Circle CenterX=318.073 CenterY=-91.7794 CenterZ=0 NormalX=0 NormalY=0 NormalZ=1 AngleXU=0 Radius=1
    g268: Circle CenterX=318.073 CenterY=-87.7794 CenterZ=0 NormalX=0 NormalY=0 NormalZ=1 AngleXU=0 Radius=1
    g269: BSplineCurve PolesCount=3 KnotsCount=2 Degree=2 IsPeriodic=0
    g270: GeomPoint X=322.073 Y=-91.7794 Z=0
    g271: GeomPoint X=318.073 Y=-87.7794 Z=0
    g272: LineSegment StartX=362.567 StartY=-89.8542 StartZ=0 EndX=321.579 EndY=-67.3492 EndZ=0
    g273: LineSegment StartX=318.073 StartY=-69.424 StartZ=0 EndX=318.073 EndY=-87.7794 EndZ=0
    g274: LineSegment StartX=322.073 StartY=-91.7794 StartZ=0 EndX=362.073 EndY=-91.7794 EndZ=0
    g275: Circle CenterX=2.07281 CenterY=124.221 CenterZ=0 NormalX=0 NormalY=0 NormalZ=1 AngleXU=0 Radius=1
    g276: Circle CenterX=1.57905 CenterY=122.295 CenterZ=0 NormalX=0 NormalY=0 NormalZ=1 AngleXU=0 Radius=1
    g277: BSplineCurve PolesCount=3 KnotsCount=2 Degree=2 IsPeriodic=0
    g278: GeomPoint X=2.07281 Y=124.221 Z=0
    g279: GeomPoint X=1.57905 Y=122.295 Z=0
    g280: Circle CenterX=42.0728 CenterY=124.221 CenterZ=0 NormalX=0 NormalY=0 NormalZ=1 AngleXU=0 Radius=1
    g281: Circle CenterX=46.0728 CenterY=124.221 CenterZ=0 NormalX=0 NormalY=0 NormalZ=1 AngleXU=0 Radius=1
    g282: Circle CenterX=46.0728 CenterY=120.221 CenterZ=0 NormalX=0 NormalY=0 NormalZ=1 AngleXU=0 Radius=1
    g283: BSplineCurve PolesCount=3 KnotsCount=2 Degree=2 IsPeriodic=0
    g284: GeomPoint X=42.0728 Y=124.221 Z=0
    g285: GeomPoint X=46.0728 Y=120.221 Z=0
    g286: Circle CenterX=46.0728 CenterY=109.865 CenterZ=0 NormalX=0 NormalY=0 NormalZ=1 AngleXU=0 Radius=1
    g287: Circle CenterX=46.0728 CenterY=105.865 CenterZ=0 NormalX=0 NormalY=0 NormalZ=1 AngleXU=0 Radius=1
    g288: Circle CenterX=42.0728 CenterY=105.865 CenterZ=0 NormalX=0 NormalY=0 NormalZ=1 AngleXU=0 Radius=1
    g289: BSplineCurve PolesCount=3 KnotsCount=2 Degree=2 IsPeriodic=0
    g290: GeomPoint X=46.0728 Y=109.865 Z=0
    g291: GeomPoint X=42.0728 Y=105.865 Z=0
    g292: Circle CenterX=35.5028 CenterY=105.865 CenterZ=0 NormalX=0 NormalY=0 NormalZ=1 AngleXU=0 Radius=1
    g293: Circle CenterX=31.5028 CenterY=105.865 CenterZ=0 NormalX=0 NormalY=0 NormalZ=1 AngleXU=0 Radius=1
    g294: Circle CenterX=27.9965 CenterY=107.79 CenterZ=0 NormalX=0 NormalY=0 NormalZ=1 AngleXU=0 Radius=1
    g295: BSplineCurve PolesCount=3 KnotsCount=2 Degree=2 IsPeriodic=0
    g296: GeomPoint X=35.5028 Y=105.865 Z=0
    g297: GeomPoint X=27.9965 Y=107.79 Z=0
    g298: LineSegment StartX=2.07281 StartY=124.221 StartZ=0 EndX=42.0728 EndY=124.221 EndZ=0
    g299: LineSegment StartX=46.0728 StartY=120.221 StartZ=0 EndX=46.0728 EndY=109.865 EndZ=0
    g300: LineSegment StartX=42.0728 StartY=105.865 StartZ=0 EndX=35.5028 EndY=105.865 EndZ=0
    g301: LineSegment StartX=27.9965 StartY=107.79 StartZ=0 EndX=1.57905 EndY=122.295 EndZ=0
    g302: Circle CenterX=42.5666 CenterY=-67.3492 CenterZ=0 NormalX=0 NormalY=0 NormalZ=1 AngleXU=0 Radius=1
    g303: Circle CenterX=46.0728 CenterY=-65.424 CenterZ=0 NormalX=0 NormalY=0 NormalZ=1 AngleXU=0 Radius=1
    g304: Circle CenterX=46.0728 CenterY=-69.424 CenterZ=0 NormalX=0 NormalY=0 NormalZ=1 AngleXU=0 Radius=1
    g305: BSplineCurve PolesCount=3 KnotsCount=2 Degree=2 IsPeriodic=0
    g306: GeomPoint X=42.5666 Y=-67.3492 Z=0
    g307: GeomPoint X=46.0728 Y=-69.424 Z=0
    g308: Circle CenterX=46.0728 CenterY=-87.7794 CenterZ=0 NormalX=0 NormalY=0 NormalZ=1 AngleXU=0 Radius=1
    g309: Circle CenterX=46.0728 CenterY=-91.7794 CenterZ=0 NormalX=0 NormalY=0 NormalZ=1 AngleXU=0 Radius=1
    g310: Circle CenterX=42.0728 CenterY=-91.7794 CenterZ=0 NormalX=0 NormalY=0 NormalZ=1 AngleXU=0 Radius=1
    g311: BSplineCurve PolesCount=3 KnotsCount=2 Degree=2 IsPeriodic=0
    g312: GeomPoint X=46.0728 Y=-87.7794 Z=0
    g313: GeomPoint X=42.0728 Y=-91.7794 Z=0
    g314: Circle CenterX=2.07281 CenterY=-91.7794 CenterZ=0 NormalX=0 NormalY=0 NormalZ=1 AngleXU=0 Radius=1
    g315: Circle CenterX=-1.92719 CenterY=-91.7794 CenterZ=0 NormalX=0 NormalY=0 NormalZ=1 AngleXU=0 Radius=1
    g316: Circle CenterX=1.57905 CenterY=-89.8542 CenterZ=0 NormalX=0 NormalY=0 NormalZ=1 AngleXU=0 Radius=1
    g317: BSplineCurve PolesCount=3 KnotsCount=2 Degree=2 IsPeriodic=0
    g318: GeomPoint X=2.07281 Y=-91.7794 Z=0
    g319: GeomPoint X=1.57905 Y=-89.8542 Z=0
    g320: LineSegment StartX=2.07281 StartY=-91.7794 StartZ=0 EndX=42.0728 EndY=-91.7794 EndZ=0
    g321: LineSegment StartX=46.0728 StartY=-87.7794 StartZ=0 EndX=46.0728 EndY=-69.424 EndZ=0
    g322: LineSegment StartX=42.5666 StartY=-67.3492 StartZ=0 EndX=1.57905 EndY=-89.8542 EndZ=0
    g323: Circle CenterX=322.073 CenterY=76.4095 CenterZ=0 NormalX=0 NormalY=0 NormalZ=1 AngleXU=0 Radius=4
    g324: BSplineCurve PolesCount=3 KnotsCount=2 Degree=2 IsPeriodic=0
    g325: GeomPoint X=318.073 Y=72.4095 Z=0
    g326: GeomPoint X=322.073 Y=76.4095 Z=0
    g327: Circle CenterX=375.073 CenterY=72.4095 CenterZ=0 NormalX=0 NormalY=0 NormalZ=1 AngleXU=0 Radius=1
    g328: Circle CenterX=375.073 CenterY=76.4095 CenterZ=0 NormalX=0 NormalY=0 NormalZ=1 AngleXU=0 Radius=1
    g329: Circle CenterX=371.073 CenterY=76.4095 CenterZ=0 NormalX=0 NormalY=0 NormalZ=1 AngleXU=0 Radius=1
    g330: BSplineCurve PolesCount=3 KnotsCount=2 Degree=2 IsPeriodic=0
    g331: GeomPoint X=375.073 Y=72.4095 Z=0
    g332: GeomPoint X=371.073 Y=76.4095 Z=0
    g333: LineSegment StartX=322.073 StartY=76.4095 StartZ=0 EndX=371.073 EndY=76.4095 EndZ=0
    g334: LineSegment StartX=318.073 StartY=72.4095 StartZ=0 EndX=318.073 EndY=-47.4805 EndZ=0
    g335: LineSegment StartX=375.073 StartY=72.4095 StartZ=0 EndX=375.073 EndY=-78.7896 EndZ=0
    g336: ArcOfCircle CenterX=-26.9272 CenterY=22.1087 CenterZ=0 NormalX=0 NormalY=0 NormalZ=1 AngleXU=0 Radius=4 StartAngle=5e-16 EndAngle=3.14159
    g337: LineSegment StartX=-22.9272 StartY=22.1087 StartZ=0 EndX=-18.9272 EndY=-83.7794 EndZ=0
    g338: LineSegment StartX=-34.9272 StartY=-83.7794 StartZ=0 EndX=-30.9272 EndY=22.1087 EndZ=0
    g339: ArcOfCircle CenterX=391.073 CenterY=22.1087 CenterZ=0 NormalX=0 NormalY=0 NormalZ=1 AngleXU=0 Radius=4 StartAngle=0 EndAngle=3.14159
    g340: LineSegment StartX=387.073 StartY=22.1087 StartZ=0 EndX=383.073 EndY=-83.7794 EndZ=0
    g341: LineSegment StartX=395.073 StartY=22.1087 StartZ=0 EndX=399.073 EndY=-83.7794 EndZ=0
    g342: Circle CenterX=-10.9272 CenterY=-78.7794 CenterZ=0 NormalX=0 NormalY=0 NormalZ=1 AngleXU=0 Radius=1
    g343: Circle CenterX=-10.9272 CenterY=-82.7794 CenterZ=0 NormalX=0 NormalY=0 NormalZ=1 AngleXU=0 Radius=1
    g344: Circle CenterX=-7.42095 CenterY=-80.8542 CenterZ=0 NormalX=0 NormalY=0 NormalZ=1 AngleXU=0 Radius=1
    g345: BSplineCurve PolesCount=3 KnotsCount=2 Degree=2 IsPeriodic=0
    g346: GeomPoint X=-10.9272 Y=-78.7794 Z=0
    g347: GeomPoint X=-7.42095 Y=-80.8542 Z=0
    g348: Circle CenterX=42.5666 CenterY=-53.4075 CenterZ=0 NormalX=0 NormalY=0 NormalZ=1 AngleXU=0 Radius=1
    g349: Circle CenterX=46.0728 CenterY=-51.4823 CenterZ=0 NormalX=0 NormalY=0 NormalZ=1 AngleXU=0 Radius=1
    g350: Circle CenterX=46.0728 CenterY=-47.4823 CenterZ=0 NormalX=0 NormalY=0 NormalZ=1 AngleXU=0 Radius=1
    g351: BSplineCurve PolesCount=3 KnotsCount=2 Degree=2 IsPeriodic=0
    g352: GeomPoint X=42.5666 Y=-53.4075 Z=0
    g353: GeomPoint X=46.0728 Y=-47.4823 Z=0
    g354: Circle CenterX=46.0728 CenterY=72.4095 CenterZ=0 NormalX=0 NormalY=0 NormalZ=1 AngleXU=0 Radius=1
    g355: Circle CenterX=46.0728 CenterY=76.4095 CenterZ=0 NormalX=0 NormalY=0 NormalZ=1 AngleXU=0 Radius=1
    g356: Circle CenterX=42.0728 CenterY=76.4095 CenterZ=0 NormalX=0 NormalY=0 NormalZ=1 AngleXU=0 Radius=1
    g357: BSplineCurve PolesCount=3 KnotsCount=2 Degree=2 IsPeriodic=0
    g358: GeomPoint X=46.0728 Y=72.4095 Z=0
    g359: GeomPoint X=42.0728 Y=76.4095 Z=0
    g360: Circle CenterX=-6.92718 CenterY=76.4095 CenterZ=0 NormalX=0 NormalY=0 NormalZ=1 AngleXU=0 Radius=1
    g361: Circle CenterX=-10.9272 CenterY=76.4095 CenterZ=0 NormalX=0 NormalY=0 NormalZ=1 AngleXU=0 Radius=1
    g362: Circle CenterX=-10.9272 CenterY=72.4095 CenterZ=0 NormalX=0 NormalY=0 NormalZ=1 AngleXU=0 Radius=1
    g363: BSplineCurve PolesCount=3 KnotsCount=2 Degree=2 IsPeriodic=0
    g364: GeomPoint X=-6.92718 Y=76.4095 Z=0
    g365: GeomPoint X=-10.9272 Y=72.4095 Z=0
    g366: LineSegment StartX=-10.9272 StartY=72.4095 StartZ=0 EndX=-10.9272 EndY=-78.7794 EndZ=0
    g367: LineSegment StartX=-7.42095 StartY=-80.8542 StartZ=0 EndX=42.5666 EndY=-53.4075 EndZ=0
    g368: LineSegment StartX=46.0728 StartY=-47.4823 StartZ=0 EndX=46.0728 EndY=72.4095 EndZ=0
    g369: LineSegment StartX=42.0728 StartY=76.4095 StartZ=0 EndX=-6.92719 EndY=76.4095 EndZ=0
    g370: LineSegment StartX=232.072 StartY=136.221 StartZ=0 EndX=232.072 EndY=-117.815 EndZ=0
    g371: LineSegment StartX=132.072 StartY=136.221 StartZ=0 EndX=132.072 EndY=-121.309 EndZ=0
    g372: LineSegment StartX=245.072 StartY=136.221 StartZ=0 EndX=245.072 EndY=-116.499 EndZ=0
    g373: LineSegment StartX=119.072 StartY=136.221 StartZ=0 EndX=119.072 EndY=-116.228 EndZ=0
    g374: LineSegment StartX=-42.9272 StartY=136.221 StartZ=0 EndX=407.073 EndY=136.221 EndZ=0
    g375: LineSegment StartX=232.072 StartY=136.221 StartZ=0 EndX=220.072 EndY=136.221 EndZ=0
    g376: LineSegment StartX=232.072 StartY=136.221 StartZ=0 EndX=232.072 EndY=124.221 EndZ=0
    g377: LineSegment StartX=220.072 StartY=136.221 StartZ=0 EndX=220.072 EndY=124.221 EndZ=0
    g378: LineSegment StartX=220.072 StartY=136.221 StartZ=0 EndX=226.072 EndY=136.221 EndZ=0
    g379: LineSegment StartX=220.072 StartY=136.221 StartZ=0 EndX=220.072 EndY=130.221 EndZ=0
    g380: LineSegment StartX=220.072 StartY=124.221 StartZ=0 EndX=226.072 EndY=124.221 EndZ=0
    g381: LineSegment StartX=232.072 StartY=124.221 StartZ=0 EndX=232.072 EndY=127.221 EndZ=0
    g382: LineSegment StartX=232.072 StartY=136.221 StartZ=0 EndX=232.072 EndY=133.221 EndZ=0
    g383-g387: Circle x5 (B-spline internal-alignment scaffolding for g388; pole/knot coordinates omitted)
    g388: BSplineCurve PolesCount=5 KnotsCount=3 Degree=3 IsPeriodic=0
    g389: GeomPoint X=232.072 Y=133.221 Z=0
    g390: GeomPoint X=223.072 Y=130.221 Z=0
    g391: GeomPoint X=232.072 Y=127.221 Z=0
    g392: LineSegment StartX=189.124 StartY=124.221 StartZ=0 EndX=302.073 EndY=124.221 EndZ=0
    g393: LineSegment StartX=132.072 StartY=136.221 StartZ=0 EndX=132.072 EndY=124.221 EndZ=0
    g394: LineSegment StartX=132.072 StartY=136.221 StartZ=0 EndX=144.072 EndY=136.221 EndZ=0
    g395: LineSegment StartX=133.749 StartY=123.285 StartZ=0 EndX=145.749 EndY=123.285 EndZ=0
    g396: LineSegment StartX=144.072 StartY=136.221 StartZ=0 EndX=144.072 EndY=124.221 EndZ=0
  constraints (669):
    c: Vertical(g0)
    c: Vertical(g1)
    c: Block(g1)
    c: Block(g0)
    c: Weight(g4) = 1
    c: Equal(g4,g5)
    c: Equal(g4,g6)
    c: InternalAlignment(g4,g7)
    c: InternalAlignment(g5,g7)
    c: InternalAlignment(g6,g7)
    c: InternalAlignment(g8,g7)
    c: InternalAlignment(g9,g7)
    c: Weight(g10) = 1
    c: Equal(g10,g11)
    c: Equal(g10,g12)
    c: InternalAlignment(g10,g13)
    c: InternalAlignment(g11,g13)
    c: InternalAlignment(g12,g13)
    c: InternalAlignment(g14,g13)
    c: InternalAlignment(g15,g13)
    c: Block(g13)
    c: Block(g7)
    c: Weight(g16) = 1
    c: Equal(g16,g17)
    c: Equal(g16,g18)
    c: InternalAlignment(g16,g19)
    c: InternalAlignment(g17,g19)
    c: InternalAlignment(g18,g19)
    c: InternalAlignment(g20,g19)
    c: InternalAlignment(g21,g19)
    c: Weight(g22) = 1
    c: Equal(g22,g23)
    c: Equal(g22,g24)
    c: InternalAlignment(g22,g25)
    c: InternalAlignment(g23,g25)
    c: InternalAlignment(g24,g25)
    c: InternalAlignment(g26,g25)
    c: InternalAlignment(g27,g25)
    c: Block(g25)
    c: Block(g19)
    c: Weight(g28) = 1
    c: Equal(g28,g29)
    c: Equal(g28,g30)
    c: InternalAlignment(g28,g31)
    c: InternalAlignment(g29,g31)
    c: InternalAlignment(g30,g31)
    c: InternalAlignment(g32,g31)
    c: InternalAlignment(g33,g31)
    c: Weight(g34) = 1
    c: Equal(g34,g35)
    c: Equal(g34,g36)
    c: InternalAlignment(g34,g37)
    c: InternalAlignment(g35,g37)
    c: InternalAlignment(g36,g37)
    c: InternalAlignment(g38,g37)
    c: InternalAlignment(g39,g37)
    c: Block(g31)
    c: Block(g37)
    c: Coincident(g40,g1)
    c: Coincident(g40,g0)
    c: Horizontal(g40)
    c: Distance(g40) = 450
    c: Weight(g41) = 1
    c: Equal(g41,g42)
    c: Equal(g41,g43)
    c: InternalAlignment(g41,g44)
    c: InternalAlignment(g42,g44)
    c: InternalAlignment(g43,g44)
    c: InternalAlignment(g45,g44)
    c: InternalAlignment(g46,g44)
    c: Block(g44)
    c: Weight(g47) = 1
    c: Equal(g47,g48)
    c: Equal(g47,g49)
    c: InternalAlignment(g47,g50)
    c: InternalAlignment(g48,g50)
    c: InternalAlignment(g49,g50)
    c: InternalAlignment(g51,g50)
    c: InternalAlignment(g52,g50)
    c: Block(g50)
    c: Weight(g53) = 1
    c: Equal(g53,g54)
    c: Equal(g53,g55)
    c: InternalAlignment(g53,g56)
    c: InternalAlignment(g54,g56)
    c: InternalAlignment(g55,g56)
    c: InternalAlignment(g57,g56)
    c: InternalAlignment(g58,g56)
    c: Block(g56)
    c: Weight(g59) = 1
    c: Equal(g59,g60)
    c: Equal(g59,g61)
    c: InternalAlignment(g59,g62)
    c: InternalAlignment(g60,g62)
    c: InternalAlignment(g61,g62)
    c: InternalAlignment(g63,g62)
    c: InternalAlignment(g64,g62)
    c: Block(g62)
    c: Weight(g65) = 1
    c: Equal(g65,g66)
    c: Equal(g65,g67)
    c: InternalAlignment(g65,g68)
    c: InternalAlignment(g66,g68)
    c: InternalAlignment(g67,g68)
    c: InternalAlignment(g69,g68)
    c: InternalAlignment(g70,g68)
    c: Weight(g71) = 1
    c: Equal(g71,g72)
    c: Equal(g71,g73)
    c: InternalAlignment(g71,g74)
    c: InternalAlignment(g72,g74)
    c: InternalAlignment(g73,g74)
    c: InternalAlignment(g75,g74)
    c: InternalAlignment(g76,g74)
    c: Block(g68)
    c: Block(g74)
    c: Coincident(g77,g68)
    c: Coincident(g77,g74)
    c: Vertical(g77)
    c: Coincident(g78,g68)
    c: Coincident(g78,g50)
    c: Coincident(g79,g50)
    c: Coincident(g79,g74)
    c: Weight(g80) = 1
    c: Equal(g80,g81)
    c: Equal(g80,g82)
    c: InternalAlignment(g80,g83)
    c: InternalAlignment(g81,g83)
    c: InternalAlignment(g82,g83)
    c: InternalAlignment(g84,g83)
    c: InternalAlignment(g85,g83)
    c: Weight(g86) = 1
    c: Equal(g86,g87)
    c: Equal(g86,g88)
    c: InternalAlignment(g86,g89)
    c: InternalAlignment(g87,g89)
    c: InternalAlignment(g88,g89)
    c: InternalAlignment(g90,g89)
    c: InternalAlignment(g91,g89)
    c: Block(g83)
    c: Block(g89)
    c: Coincident(g92,g83)
    c: Coincident(g92,g89)
    c: Vertical(g92)
    c: Coincident(g93,g83)
    c: Coincident(g93,g44)
    c: Coincident(g94,g44)
    c: Coincident(g94,g89)
    c: Weight(g95) = 1
    c: Equal(g95,g96)
    c: Equal(g95,g97)
    c: InternalAlignment(g95,g98)
    c: InternalAlignment(g96,g98)
    c: InternalAlignment(g97,g98)
    c: InternalAlignment(g99,g98)
    c: InternalAlignment(g100,g98)
    c: Weight(g101) = 1
    c: Equal(g101,g102)
    c: Equal(g101,g103)
    c: InternalAlignment(g101,g104)
    c: InternalAlignment(g102,g104)
    c: InternalAlignment(g103,g104)
    c: InternalAlignment(g105,g104)
    c: InternalAlignment(g106,g104)
    c: Block(g98)
    c: Block(g104)
    c: Coincident(g107,g98)
    c: Coincident(g107,g104)
    c: Vertical(g107)
    c: Coincident(g108,g104)
    c: Coincident(g108,g62)
    c: Coincident(g109,g62)
    c: Coincident(g109,g98)
    c: Weight(g110) = 1
    c: Equal(g110,g111)
    c: Equal(g110,g112)
    c: InternalAlignment(g110,g113)
    c: InternalAlignment(g111,g113)
    c: InternalAlignment(g112,g113)
    c: InternalAlignment(g114,g113)
    c: InternalAlignment(g115,g113)
    c: Weight(g116) = 1
    c: Equal(g116,g117)
    c: Equal(g116,g118)
    c: InternalAlignment(g116,g119)
    c: InternalAlignment(g117,g119)
    c: InternalAlignment(g118,g119)
    c: InternalAlignment(g120,g119)
    c: InternalAlignment(g121,g119)
    c: Block(g113)
    c: Block(g119)
    c: Coincident(g122,g113)
    c: Coincident(g122,g119)
    c: Vertical(g122)
    c: Coincident(g123,g119)
    c: Coincident(g123,g56)
    c: Coincident(g124,g56)
    c: Coincident(g124,g113)
    c: Weight(g125) = 1
    c: Equal(g125,g126)
    c: Equal(g125,g127)
    c: InternalAlignment(g125,g128)
    c: InternalAlignment(g126,g128)
    c: InternalAlignment(g127,g128)
    c: InternalAlignment(g129,g128)
    c: InternalAlignment(g130,g128)
    c: Weight(g131) = 1
    c: Equal(g131,g132)
    c: Equal(g131,g133)
    c: InternalAlignment(g131,g134)
    c: InternalAlignment(g132,g134)
    c: InternalAlignment(g133,g134)
    c: InternalAlignment(g135,g134)
    c: InternalAlignment(g136,g134)
    c: Weight(g137) = 1
    c: Equal(g137,g138)
    c: Equal(g137,g139)
    c: InternalAlignment(g137,g140)
    c: InternalAlignment(g138,g140)
    c: InternalAlignment(g139,g140)
    c: InternalAlignment(g141,g140)
    c: InternalAlignment(g142,g140)
    c: Weight(g143) = 1
    c: Equal(g143,g144)
    c: Equal(g143,g145)
    c: InternalAlignment(g143,g146)
    c: InternalAlignment(g144,g146)
    c: InternalAlignment(g145,g146)
    c: InternalAlignment(g147,g146)
    c: InternalAlignment(g148,g146)
    c: Block(g146)
    c: Block(g140)
    c: Block(g134)
    c: Block(g128)
    c: Coincident(g149,g25)
    c: Coincident(g149,g146)
    c: Coincident(g150,g146)
    c: Coincident(g150,g140)
    c: Horizontal(g150)
    c: Coincident(g151,g140)
    c: Coincident(g151,g25)
    c: Vertical(g151)
    c: Coincident(g152,g19)
    c: Coincident(g152,g134)
    c: Vertical(g152)
    c: Coincident(g153,g134)
    c: Coincident(g153,g128)
    c: Horizontal(g153)
    c: Coincident(g154,g128)
    c: Coincident(g154,g19)
    c: Weight(g155) = 1
    c: Equal(g155,g156)
    c: Equal(g155,g157)
    c: InternalAlignment(g155,g158)
    c: InternalAlignment(g156,g158)
    c: InternalAlignment(g157,g158)
    c: InternalAlignment(g159,g158)
    c: InternalAlignment(g160,g158)
    c: Weight(g161) = 1
    c: Equal(g161,g162)
    c: Equal(g161,g163)
    c: InternalAlignment(g161,g164)
    c: InternalAlignment(g162,g164)
    c: InternalAlignment(g163,g164)
    c: InternalAlignment(g165,g164)
    c: InternalAlignment(g166,g164)
    c: Weight(g167) = 1
    c: Equal(g167,g168)
    c: Equal(g167,g169)
    c: InternalAlignment(g167,g170)
    c: InternalAlignment(g168,g170)
    c: InternalAlignment(g169,g170)
    c: InternalAlignment(g171,g170)
    c: InternalAlignment(g172,g170)
    c: Weight(g173) = 1
    c: Equal(g173,g174)
    c: Equal(g173,g175)
    c: InternalAlignment(g173,g176)
    c: InternalAlignment(g174,g176)
    c: InternalAlignment(g175,g176)
    c: InternalAlignment(g177,g176)
    c: InternalAlignment(g178,g176)
    c: Block(g176)
    c: Block(g170)
    c: Block(g164)
    c: Block(g158)
    c: Coincident(g179,g170)
    c: Coincident(g179,g7)
    c: Vertical(g179)
    c: Coincident(g180,g13)
    c: Coincident(g180,g164)
    c: Vertical(g180)
    c: Coincident(g181,g158)
    c: Coincident(g181,g13)
    c: Coincident(g182,g7)
    c: Weight(g183) = 1
    c: Equal(g183,g184)
    c: Equal(g183,g185)
    c: InternalAlignment(g183,g186)
    c: InternalAlignment(g184,g186)
    c: InternalAlignment(g185,g186)
    c: InternalAlignment(g187,g186)
    c: InternalAlignment(g188,g186)
    c: Weight(g189) = 1
    c: Equal(g189,g190)
    c: Equal(g189,g191)
    c: InternalAlignment(g189,g192)
    c: InternalAlignment(g190,g192)
    c: InternalAlignment(g191,g192)
    c: InternalAlignment(g193,g192)
    c: InternalAlignment(g194,g192)
    c: Block(g192)
    c: Block(g186)
    c: Coincident(g195,g192)
    c: Coincident(g195,g31)
    c: Coincident(g196,g31)
    c: Coincident(g196,g186)
    c: Coincident(g197,g186)
    c: Coincident(g197,g192)
    c: Vertical(g197)
    c: Weight(g198) = 1
    c: Equal(g198,g199)
    c: Equal(g198,g200)
    c: InternalAlignment(g198,g201)
    c: InternalAlignment(g199,g201)
    c: InternalAlignment(g200,g201)
    c: InternalAlignment(g202,g201)
    c: InternalAlignment(g203,g201)
    c: Weight(g204) = 1
    c: Equal(g204,g205)
    c: Equal(g204,g206)
    c: InternalAlignment(g204,g207)
    c: InternalAlignment(g205,g207)
    c: InternalAlignment(g206,g207)
    c: InternalAlignment(g208,g207)
    c: InternalAlignment(g209,g207)
    c: Block(g207)
    c: Block(g201)
    c: Coincident(g210,g201)
    c: Coincident(g210,g37)
    c: Coincident(g211,g37)
    c: Coincident(g211,g207)
    c: Coincident(g212,g207)
    c: Coincident(g212,g201)
    c: Vertical(g212)
    c: Horizontal(g213)
    c: Block(g213)
    c: Vertical(g214)
    c: Block(g214)
    c: Block(g215)
    c: Weight(g216) = 1
    c: Equal(g216,g217)
    c: Equal(g216,g218)
    c: InternalAlignment(g216,g219)
    c: InternalAlignment(g217,g219)
    c: InternalAlignment(g218,g219)
    c: InternalAlignment(g220,g219)
    c: InternalAlignment(g221,g219)
    c: Weight(g222) = 1
    c: Equal(g222,g223)
    c: Equal(g222,g224)
    c: InternalAlignment(g222,g225)
    c: InternalAlignment(g223,g225)
    c: InternalAlignment(g224,g225)
    c: InternalAlignment(g226,g225)
    c: InternalAlignment(g227,g225)
    c: Weight(g228) = 1
    c: Equal(g228,g229)
    c: Equal(g228,g230)
    c: InternalAlignment(g228,g231)
    c: InternalAlignment(g229,g231)
    c: InternalAlignment(g230,g231)
    c: InternalAlignment(g232,g231)
    c: InternalAlignment(g233,g231)
    c: Weight(g234) = 1
    c: Equal(g234,g235)
    c: Equal(g234,g236)
    c: InternalAlignment(g234,g237)
    c: InternalAlignment(g235,g237)
    c: InternalAlignment(g236,g237)
    c: InternalAlignment(g238,g237)
    c: InternalAlignment(g239,g237)
    c: Block(g219)
    c: Block(g225)
    c: Block(g231)
    c: Block(g237)
    c: Coincident(g240,g225)
    c: Coincident(g240,g219)
    c: Horizontal(g240)
    c: Block(g182)
    c: Weight(g241) = 1
    c: Equal(g241,g242)
    c: Equal(g241,g243)
    c: InternalAlignment(g241,g244)
    c: InternalAlignment(g242,g244)
    c: InternalAlignment(g243,g244)
    c: InternalAlignment(g245,g244)
    c: InternalAlignment(g246,g244)
    c: Weight(g247) = 1
    c: Equal(g247,g248)
    c: Equal(g247,g249)
    c: InternalAlignment(g247,g250)
    c: InternalAlignment(g248,g250)
    c: InternalAlignment(g249,g250)
    c: InternalAlignment(g251,g250)
    c: InternalAlignment(g252,g250)
    c: Block(g244)
    c: Block(g250)
    c: Coincident(g253,g244)
    c: Coincident(g253,g250)
    c: Weight(g254) = 1
    c: Equal(g254,g255)
    c: Equal(g254,g256)
    c: InternalAlignment(g254,g257)
    c: InternalAlignment(g255,g257)
    c: InternalAlignment(g256,g257)
    c: InternalAlignment(g258,g257)
    c: InternalAlignment(g259,g257)
    c: Weight(g260) = 1
    c: Equal(g260,g261)
    c: Equal(g260,g262)
    c: InternalAlignment(g260,g263)
    c: InternalAlignment(g261,g263)
    c: InternalAlignment(g262,g263)
    c: InternalAlignment(g264,g263)
    c: InternalAlignment(g265,g263)
    c: Weight(g266) = 1
    c: Equal(g266,g267)
    c: Equal(g266,g268)
    c: InternalAlignment(g266,g269)
    c: InternalAlignment(g267,g269)
    c: InternalAlignment(g268,g269)
    c: InternalAlignment(g270,g269)
    c: InternalAlignment(g271,g269)
    c: Block(g269)
    c: Block(g263)
    c: Block(g257)
    c: Coincident(g272,g263)
    c: Coincident(g272,g257)
    c: Coincident(g273,g257)
    c: Coincident(g273,g269)
    c: Vertical(g273)
    c: Coincident(g274,g269)
    c: Coincident(g274,g263)
    c: Horizontal(g274)
    c: Weight(g275) = 1
    c: Equal(g275,g276)
    c: InternalAlignment(g275,g277)
    c: InternalAlignment(g276,g277)
    c: InternalAlignment(g278,g277)
    c: InternalAlignment(g279,g277)
    c: Weight(g280) = 1
    c: InternalAlignment(g281,g283)
    c: InternalAlignment(g282,g283)
    c: InternalAlignment(g284,g283)
    c: InternalAlignment(g285,g283)
    c: Weight(g286) = 1
    c: Equal(g286,g287)
    c: Equal(g286,g288)
    c: InternalAlignment(g286,g289)
    c: InternalAlignment(g287,g289)
    c: InternalAlignment(g288,g289)
    c: InternalAlignment(g290,g289)
    c: InternalAlignment(g291,g289)
    c: Equal(g292,g293)
    c: Equal(g292,g294)
    c: InternalAlignment(g292,g295)
    c: InternalAlignment(g293,g295)
    c: InternalAlignment(g294,g295)
    c: InternalAlignment(g296,g295)
    c: InternalAlignment(g297,g295)
    c: Block(g283)
    c: Block(g289)
    c: Block(g295)
    c: Block(g277)
    c: Coincident(g298,g277)
    c: Coincident(g298,g283)
    c: Horizontal(g298)
    c: Coincident(g299,g283)
    c: Coincident(g299,g289)
    c: Vertical(g299)
    c: Coincident(g300,g289)
    c: Coincident(g300,g295)
    c: Horizontal(g300)
    c: Coincident(g301,g295)
    c: Coincident(g301,g277)
    c: Weight(g302) = 1
    c: Equal(g302,g303)
    c: Equal(g302,g304)
    c: InternalAlignment(g302,g305)
    c: InternalAlignment(g303,g305)
    c: InternalAlignment(g304,g305)
    c: InternalAlignment(g306,g305)
    c: InternalAlignment(g307,g305)
    c: Weight(g308) = 1
    c: Equal(g308,g309)
    c: Equal(g308,g310)
    c: InternalAlignment(g308,g311)
    c: InternalAlignment(g309,g311)
    c: InternalAlignment(g310,g311)
    c: InternalAlignment(g312,g311)
    c: Weight(g314) = 1
    c: Equal(g314,g315)
    c: Equal(g314,g316)
    c: InternalAlignment(g314,g317)
    c: InternalAlignment(g315,g317)
    c: InternalAlignment(g316,g317)
    c: InternalAlignment(g318,g317)
    c: InternalAlignment(g319,g317)
    c: Block(g317)
    c: Block(g311)
    c: Block(g305)
    c: Coincident(g320,g317)
    c: Coincident(g320,g311)
    c: Horizontal(g320)
    c: Coincident(g321,g311)
    c: Coincident(g321,g305)
    c: Vertical(g321)
    c: Coincident(g322,g305)
    c: Coincident(g322,g317)
    c: InternalAlignment(g323,g324)
    c: InternalAlignment(g325,g324)
    c: InternalAlignment(g326,g324)
    c: Block(g324)
    c: Equal(g327,g328)
    c: Equal(g327,g329)
    c: InternalAlignment(g327,g330)
    c: InternalAlignment(g328,g330)
    c: InternalAlignment(g329,g330)
    c: InternalAlignment(g331,g330)
    c: InternalAlignment(g332,g330)
    c: Block(g330)
    c: Coincident(g333,g324)
    c: Horizontal(g333)
    c: Block(g333)
    c: Coincident(g334,g324)
    c: Coincident(g334,g250)
    c: Vertical(g334)
    c: Coincident(g335,g330)
    c: Coincident(g335,g244)
    c: Vertical(g335)
    c: Block(g336)
    c: Block(g2)
    c: Distance(g334) = 119.89
    c: Coincident(g337,g336)
    c: Coincident(g337,g2)
    c: Coincident(g338,g2)
    c: Coincident(g338,g336)
    c: Block(g3)
    c: Block(g339)
    c: Coincident(g340,g339)
    c: Coincident(g340,g3)
    c: Coincident(g341,g339)
    c: Coincident(g341,g3)
    c: Block(g341)
    c: Block(g340)
    c: Weight(g342) = 1
    c: Equal(g342,g343)
    c: Equal(g342,g344)
    c: InternalAlignment(g342,g345)
    c: InternalAlignment(g343,g345)
    c: InternalAlignment(g344,g345)
    c: InternalAlignment(g346,g345)
    c: InternalAlignment(g347,g345)
    c: Weight(g348) = 1
    c: Equal(g348,g349)
    c: Equal(g348,g350)
    c: InternalAlignment(g348,g351)
    c: InternalAlignment(g349,g351)
    c: InternalAlignment(g350,g351)
    c: InternalAlignment(g352,g351)
    c: InternalAlignment(g353,g351)
    c: Weight(g354) = 1
    c: Equal(g354,g355)
    c: Equal(g354,g356)
    c: InternalAlignment(g354,g357)
    c: InternalAlignment(g355,g357)
    c: InternalAlignment(g356,g357)
    c: InternalAlignment(g358,g357)
    c: InternalAlignment(g359,g357)
    c: Weight(g360) = 1
    c: Equal(g360,g361)
    c: Equal(g360,g362)
    c: InternalAlignment(g360,g363)
    c: InternalAlignment(g361,g363)
    c: InternalAlignment(g362,g363)
    c: InternalAlignment(g364,g363)
    c: InternalAlignment(g365,g363)
    c: Block(g363)
    c: Block(g357)
    c: Block(g351)
    c: Block(g345)
    c: Coincident(g366,g363)
    c: Coincident(g366,g345)
    c: Vertical(g366)
    c: Coincident(g367,g345)
    c: Coincident(g367,g351)
    c: Coincident(g368,g351)
    c: Coincident(g368,g357)
    c: Vertical(g368)
    c: Coincident(g369,g357)
    c: Coincident(g369,g363)
    c: Horizontal(g369)
    c: Vertical(g370)
    c: Vertical(g371)
    c: Vertical(g372)
    c: Vertical(g373)
    c: Coincident(g374,g0)
    c: Coincident(g374,g1)
    c: Horizontal(g374)
    c: Block(g374)
    c: Distance(g374) = 450
    c: Block(g372)
    c: Block(g370)
    c: Block(g371)
    c: Block(g373)
    c: Distance(g0) = 240
    c: Horizontal(g375)
    c: Distance(g375) = 12
    c: Coincident(g375,g370)
    c: Vertical(g376)
    c: Distance(g376) = 12
    c: Coincident(g376,g370)
    c: Coincident(g377,g375)
    c: Vertical(g377)
    c: Horizontal(g378)
    c: Vertical(g379)
    c: Distance(g379) = 6
    c: Coincident(g379,g375)
    c: Coincident(g378,g375)
    c: Block(g377)
    c: Coincident(g380,g377)
    c: Horizontal(g380)
    c: Distance(g380) = 6
    c: Vertical(g381)
    c: Distance(g381) = 3
    c: Vertical(g382)
    c: Distance(g382) = 3
    c: Coincident(g382,g370)
    c: Coincident(g376,g381)
    c: Coincident(g388,g382)
    c: Weight(g383) = 1
    c: Equal(g383,g384)
    c: Coincident(g384,g378)
    c: Equal(g383,g385)
    c: Coincident(g385,g379)
    c: Equal(g383,g386)
    c: Coincident(g386,g380)
    c: Equal(g383,g387)
    c: Coincident(g388,g381)
    c: InternalAlignment(g383-g387 -> g388) x5
    c: InternalAlignment(g389,g388)
    c: InternalAlignment(g390,g388)
    c: InternalAlignment(g391,g388)
    c: Coincident(g392,g164)
    c: Coincident(g392,g158)
    c: Horizontal(g392)
    c: Block(g388)
    c: Vertical(g393)
    c: Distance(g393) = 12
    c: Coincident(g393,g371)
    c: Horizontal(g394)
    c: Distance(g394) = 12
    c: Horizontal(g395)
    c: Equal(g394,g395) = 12
    c: Coincident(g394,g371)
    c: Coincident(g396,g394)
    c: Vertical(g396)
    c: Distance(g396) = 12
FEATURE [Part::Extrusion] Extrude005
  Base = -> Sketch003
  Dir = (0,0,1)
  DirMode = 2
  FaceMakerClass = Part::FaceMakerBullseye
  LengthFwd = 24
  LengthRev = 0
  Solid = true
  Symmetric = false
